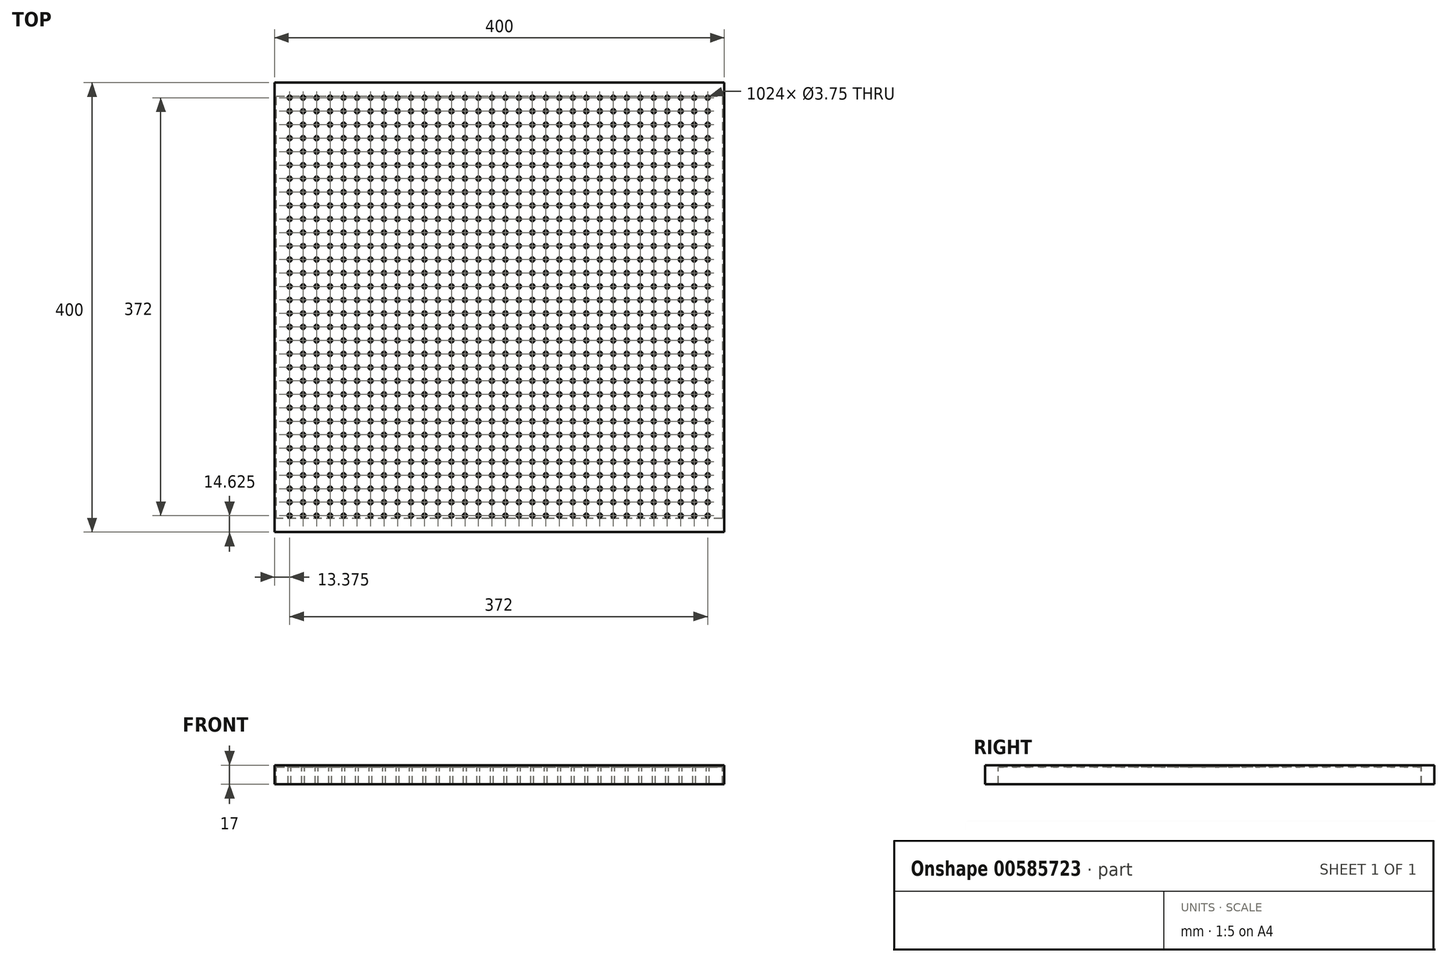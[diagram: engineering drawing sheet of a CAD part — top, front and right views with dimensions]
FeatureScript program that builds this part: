
annotation { "Feature Type Name" : "Feature", "Feature Type Description" : "" }
export const myFeature = defineFeature(function(context is Context, id is Id, definition is map)
    precondition{}
    {
        {
            var Q0;
            Q0=qCreatedBy(makeId("Top.planeOp"),FACE);
            var sketch = newSketch(context, id + "F0", { "sketchPlane" : qUnion([Q0])});
            skLineSegment(sketch, "E0.bottom", {"start": v(200, 200) * mm, "end": v(-200, 200) * mm});
            skLineSegment(sketch, "E0.top", {"start": v(200, -200) * mm, "end": v(-200, -200) * mm});
            skLineSegment(sketch, "E0.left", {"start": v(200, 200) * mm, "end": v(200, -200) * mm});
            skLineSegment(sketch, "E0.right", {"start": v(-200, 200) * mm, "end": v(-200, -200) * mm});
            skPoint(sketch, "E0.middle", {"position": v(0, 0) * mm});
            skSolve(sketch);
        }
        {
            var Q0;
            Q0=makeQuery(id+"F0.imprint","IMPRINT",FACE,{"disambiguationData":[TD([[makeQuery(id+"F0.imprint","IMPRINT",EDGE,{"derivedFrom":sQuery(id+"F0.wireOp",EDGE,"E0.bottom")}),1.0]])]});
            extrude(context, id + "F1", {"entities" : qUnion([Q0]), "depth" : 1.5 * mm, "offsetDistance" : 25 * mm});
        }
        {
            var Q0;
            Q0=makeQuery(id+"F1.opExtrude","CAP_FACE",FACE,{"disambiguationData":[OSD([sQuery(id+"F0.wireOp",EDGE,"E0.bottom"),sQuery(id+"F0.wireOp",EDGE,"E0.top"),sQuery(id+"F0.wireOp",EDGE,"E0.left"),sQuery(id+"F0.wireOp",EDGE,"E0.right")])],"isStart":false});
            var sketch = newSketch(context, id + "F2", { "sketchPlane" : qUnion([Q0])});
            skCircle(sketch, "E1", {"center": v(-186.63, 186.62) * mm, "radius": 1.88 * mm});
            skCircle(sketch, "E2.0.1.0", {"center": v(-186.63, 174.62) * mm, "radius": 1.88 * mm});
            skCircle(sketch, "E2.0.2.0", {"center": v(-186.63, 162.62) * mm, "radius": 1.88 * mm});
            skCircle(sketch, "E2.0.3.0", {"center": v(-186.63, 150.62) * mm, "radius": 1.88 * mm});
            skCircle(sketch, "E2.0.4.0", {"center": v(-186.63, 138.62) * mm, "radius": 1.88 * mm});
            skCircle(sketch, "E2.0.5.0", {"center": v(-186.63, 126.62) * mm, "radius": 1.88 * mm});
            skCircle(sketch, "E2.0.6.0", {"center": v(-186.63, 114.62) * mm, "radius": 1.88 * mm});
            skCircle(sketch, "E2.0.7.0", {"center": v(-186.63, 102.62) * mm, "radius": 1.88 * mm});
            skCircle(sketch, "E2.0.8.0", {"center": v(-186.63, 90.62) * mm, "radius": 1.88 * mm});
            skCircle(sketch, "E2.0.9.0", {"center": v(-186.63, 78.62) * mm, "radius": 1.88 * mm});
            skCircle(sketch, "E2.0.10.0", {"center": v(-186.63, 66.62) * mm, "radius": 1.88 * mm});
            skCircle(sketch, "E2.0.11.0", {"center": v(-186.63, 54.62) * mm, "radius": 1.88 * mm});
            skCircle(sketch, "E2.0.12.0", {"center": v(-186.63, 42.62) * mm, "radius": 1.88 * mm});
            skCircle(sketch, "E2.0.13.0", {"center": v(-186.63, 30.62) * mm, "radius": 1.88 * mm});
            skCircle(sketch, "E2.0.14.0", {"center": v(-186.63, 18.62) * mm, "radius": 1.88 * mm});
            skCircle(sketch, "E2.0.15.0", {"center": v(-186.63, 6.62) * mm, "radius": 1.88 * mm});
            skCircle(sketch, "E2.0.16.0", {"center": v(-186.63, -5.38) * mm, "radius": 1.88 * mm});
            skCircle(sketch, "E2.0.17.0", {"center": v(-186.63, -17.38) * mm, "radius": 1.88 * mm});
            skCircle(sketch, "E2.0.18.0", {"center": v(-186.63, -29.38) * mm, "radius": 1.88 * mm});
            skCircle(sketch, "E2.0.19.0", {"center": v(-186.63, -41.38) * mm, "radius": 1.88 * mm});
            skCircle(sketch, "E2.0.20.0", {"center": v(-186.63, -53.38) * mm, "radius": 1.88 * mm});
            skCircle(sketch, "E2.0.21.0", {"center": v(-186.63, -65.38) * mm, "radius": 1.88 * mm});
            skCircle(sketch, "E2.0.22.0", {"center": v(-186.63, -77.38) * mm, "radius": 1.88 * mm});
            skCircle(sketch, "E2.0.23.0", {"center": v(-186.63, -89.38) * mm, "radius": 1.88 * mm});
            skCircle(sketch, "E2.0.24.0", {"center": v(-186.63, -101.38) * mm, "radius": 1.88 * mm});
            skCircle(sketch, "E2.0.25.0", {"center": v(-186.63, -113.38) * mm, "radius": 1.88 * mm});
            skCircle(sketch, "E2.0.26.0", {"center": v(-186.63, -125.38) * mm, "radius": 1.88 * mm});
            skCircle(sketch, "E2.0.27.0", {"center": v(-186.63, -137.38) * mm, "radius": 1.88 * mm});
            skCircle(sketch, "E2.0.28.0", {"center": v(-186.63, -149.38) * mm, "radius": 1.88 * mm});
            skCircle(sketch, "E2.0.29.0", {"center": v(-186.63, -161.38) * mm, "radius": 1.88 * mm});
            skCircle(sketch, "E2.0.30.0", {"center": v(-186.63, -173.38) * mm, "radius": 1.88 * mm});
            skCircle(sketch, "E2.0.31.0", {"center": v(-186.63, -185.38) * mm, "radius": 1.88 * mm});
            skCircle(sketch, "E2.1.0.0", {"center": v(-174.63, 186.62) * mm, "radius": 1.88 * mm});
            skCircle(sketch, "E2.1.1.0", {"center": v(-174.63, 174.62) * mm, "radius": 1.88 * mm});
            skCircle(sketch, "E2.1.2.0", {"center": v(-174.63, 162.62) * mm, "radius": 1.88 * mm});
            skCircle(sketch, "E2.1.3.0", {"center": v(-174.63, 150.62) * mm, "radius": 1.88 * mm});
            skCircle(sketch, "E2.1.4.0", {"center": v(-174.63, 138.62) * mm, "radius": 1.88 * mm});
            skCircle(sketch, "E2.1.5.0", {"center": v(-174.63, 126.62) * mm, "radius": 1.88 * mm});
            skCircle(sketch, "E2.1.6.0", {"center": v(-174.63, 114.62) * mm, "radius": 1.88 * mm});
            skCircle(sketch, "E2.1.7.0", {"center": v(-174.63, 102.62) * mm, "radius": 1.88 * mm});
            skCircle(sketch, "E2.1.8.0", {"center": v(-174.63, 90.62) * mm, "radius": 1.88 * mm});
            skCircle(sketch, "E2.1.9.0", {"center": v(-174.63, 78.62) * mm, "radius": 1.88 * mm});
            skCircle(sketch, "E2.1.10.0", {"center": v(-174.63, 66.62) * mm, "radius": 1.88 * mm});
            skCircle(sketch, "E2.1.11.0", {"center": v(-174.63, 54.62) * mm, "radius": 1.88 * mm});
            skCircle(sketch, "E2.1.12.0", {"center": v(-174.63, 42.62) * mm, "radius": 1.88 * mm});
            skCircle(sketch, "E2.1.13.0", {"center": v(-174.63, 30.62) * mm, "radius": 1.88 * mm});
            skCircle(sketch, "E2.1.14.0", {"center": v(-174.63, 18.62) * mm, "radius": 1.88 * mm});
            skCircle(sketch, "E2.1.15.0", {"center": v(-174.63, 6.62) * mm, "radius": 1.88 * mm});
            skCircle(sketch, "E2.1.16.0", {"center": v(-174.63, -5.38) * mm, "radius": 1.88 * mm});
            skCircle(sketch, "E2.1.17.0", {"center": v(-174.63, -17.38) * mm, "radius": 1.88 * mm});
            skCircle(sketch, "E2.1.18.0", {"center": v(-174.63, -29.38) * mm, "radius": 1.88 * mm});
            skCircle(sketch, "E2.1.19.0", {"center": v(-174.63, -41.38) * mm, "radius": 1.88 * mm});
            skCircle(sketch, "E2.1.20.0", {"center": v(-174.63, -53.38) * mm, "radius": 1.88 * mm});
            skCircle(sketch, "E2.1.21.0", {"center": v(-174.63, -65.38) * mm, "radius": 1.88 * mm});
            skCircle(sketch, "E2.1.22.0", {"center": v(-174.63, -77.38) * mm, "radius": 1.88 * mm});
            skCircle(sketch, "E2.1.23.0", {"center": v(-174.63, -89.38) * mm, "radius": 1.88 * mm});
            skCircle(sketch, "E2.1.24.0", {"center": v(-174.63, -101.38) * mm, "radius": 1.88 * mm});
            skCircle(sketch, "E2.1.25.0", {"center": v(-174.63, -113.38) * mm, "radius": 1.88 * mm});
            skCircle(sketch, "E2.1.26.0", {"center": v(-174.63, -125.38) * mm, "radius": 1.88 * mm});
            skCircle(sketch, "E2.1.27.0", {"center": v(-174.63, -137.38) * mm, "radius": 1.88 * mm});
            skCircle(sketch, "E2.1.28.0", {"center": v(-174.63, -149.38) * mm, "radius": 1.88 * mm});
            skCircle(sketch, "E2.1.29.0", {"center": v(-174.63, -161.38) * mm, "radius": 1.88 * mm});
            skCircle(sketch, "E2.1.30.0", {"center": v(-174.63, -173.38) * mm, "radius": 1.88 * mm});
            skCircle(sketch, "E2.1.31.0", {"center": v(-174.63, -185.38) * mm, "radius": 1.88 * mm});
            skCircle(sketch, "E2.2.0.0", {"center": v(-162.63, 186.62) * mm, "radius": 1.88 * mm});
            skCircle(sketch, "E2.2.1.0", {"center": v(-162.63, 174.62) * mm, "radius": 1.88 * mm});
            skCircle(sketch, "E2.2.2.0", {"center": v(-162.63, 162.62) * mm, "radius": 1.88 * mm});
            skCircle(sketch, "E2.2.3.0", {"center": v(-162.63, 150.62) * mm, "radius": 1.88 * mm});
            skCircle(sketch, "E2.2.4.0", {"center": v(-162.63, 138.62) * mm, "radius": 1.88 * mm});
            skCircle(sketch, "E2.2.5.0", {"center": v(-162.63, 126.62) * mm, "radius": 1.88 * mm});
            skCircle(sketch, "E2.2.6.0", {"center": v(-162.63, 114.62) * mm, "radius": 1.88 * mm});
            skCircle(sketch, "E2.2.7.0", {"center": v(-162.63, 102.62) * mm, "radius": 1.88 * mm});
            skCircle(sketch, "E2.2.8.0", {"center": v(-162.63, 90.62) * mm, "radius": 1.88 * mm});
            skCircle(sketch, "E2.2.9.0", {"center": v(-162.63, 78.62) * mm, "radius": 1.88 * mm});
            skCircle(sketch, "E2.2.10.0", {"center": v(-162.63, 66.62) * mm, "radius": 1.88 * mm});
            skCircle(sketch, "E2.2.11.0", {"center": v(-162.63, 54.62) * mm, "radius": 1.88 * mm});
            skCircle(sketch, "E2.2.12.0", {"center": v(-162.63, 42.62) * mm, "radius": 1.88 * mm});
            skCircle(sketch, "E2.2.13.0", {"center": v(-162.63, 30.62) * mm, "radius": 1.88 * mm});
            skCircle(sketch, "E2.2.14.0", {"center": v(-162.63, 18.62) * mm, "radius": 1.88 * mm});
            skCircle(sketch, "E2.2.15.0", {"center": v(-162.63, 6.62) * mm, "radius": 1.88 * mm});
            skCircle(sketch, "E2.2.16.0", {"center": v(-162.63, -5.38) * mm, "radius": 1.88 * mm});
            skCircle(sketch, "E2.2.17.0", {"center": v(-162.63, -17.38) * mm, "radius": 1.88 * mm});
            skCircle(sketch, "E2.2.18.0", {"center": v(-162.63, -29.38) * mm, "radius": 1.88 * mm});
            skCircle(sketch, "E2.2.19.0", {"center": v(-162.63, -41.38) * mm, "radius": 1.88 * mm});
            skCircle(sketch, "E2.2.20.0", {"center": v(-162.63, -53.38) * mm, "radius": 1.88 * mm});
            skCircle(sketch, "E2.2.21.0", {"center": v(-162.63, -65.38) * mm, "radius": 1.88 * mm});
            skCircle(sketch, "E2.2.22.0", {"center": v(-162.63, -77.38) * mm, "radius": 1.88 * mm});
            skCircle(sketch, "E2.2.23.0", {"center": v(-162.63, -89.38) * mm, "radius": 1.88 * mm});
            skCircle(sketch, "E2.2.24.0", {"center": v(-162.63, -101.38) * mm, "radius": 1.88 * mm});
            skCircle(sketch, "E2.2.25.0", {"center": v(-162.63, -113.38) * mm, "radius": 1.88 * mm});
            skCircle(sketch, "E2.2.26.0", {"center": v(-162.63, -125.38) * mm, "radius": 1.88 * mm});
            skCircle(sketch, "E2.2.27.0", {"center": v(-162.63, -137.38) * mm, "radius": 1.88 * mm});
            skCircle(sketch, "E2.2.28.0", {"center": v(-162.63, -149.38) * mm, "radius": 1.88 * mm});
            skCircle(sketch, "E2.2.29.0", {"center": v(-162.63, -161.38) * mm, "radius": 1.88 * mm});
            skCircle(sketch, "E2.2.30.0", {"center": v(-162.63, -173.38) * mm, "radius": 1.88 * mm});
            skCircle(sketch, "E2.2.31.0", {"center": v(-162.63, -185.38) * mm, "radius": 1.88 * mm});
            skCircle(sketch, "E2.3.0.0", {"center": v(-150.63, 186.62) * mm, "radius": 1.88 * mm});
            skCircle(sketch, "E2.3.1.0", {"center": v(-150.63, 174.62) * mm, "radius": 1.88 * mm});
            skCircle(sketch, "E2.3.2.0", {"center": v(-150.63, 162.62) * mm, "radius": 1.88 * mm});
            skCircle(sketch, "E2.3.3.0", {"center": v(-150.63, 150.62) * mm, "radius": 1.88 * mm});
            skCircle(sketch, "E2.3.4.0", {"center": v(-150.63, 138.62) * mm, "radius": 1.88 * mm});
            skCircle(sketch, "E2.3.5.0", {"center": v(-150.63, 126.62) * mm, "radius": 1.88 * mm});
            skCircle(sketch, "E2.3.6.0", {"center": v(-150.63, 114.62) * mm, "radius": 1.88 * mm});
            skCircle(sketch, "E2.3.7.0", {"center": v(-150.63, 102.62) * mm, "radius": 1.88 * mm});
            skCircle(sketch, "E2.3.8.0", {"center": v(-150.63, 90.62) * mm, "radius": 1.88 * mm});
            skCircle(sketch, "E2.3.9.0", {"center": v(-150.63, 78.62) * mm, "radius": 1.88 * mm});
            skCircle(sketch, "E2.3.10.0", {"center": v(-150.63, 66.62) * mm, "radius": 1.88 * mm});
            skCircle(sketch, "E2.3.11.0", {"center": v(-150.63, 54.62) * mm, "radius": 1.88 * mm});
            skCircle(sketch, "E2.3.12.0", {"center": v(-150.63, 42.62) * mm, "radius": 1.88 * mm});
            skCircle(sketch, "E2.3.13.0", {"center": v(-150.63, 30.62) * mm, "radius": 1.88 * mm});
            skCircle(sketch, "E2.3.14.0", {"center": v(-150.63, 18.62) * mm, "radius": 1.88 * mm});
            skCircle(sketch, "E2.3.15.0", {"center": v(-150.63, 6.62) * mm, "radius": 1.88 * mm});
            skCircle(sketch, "E2.3.16.0", {"center": v(-150.63, -5.38) * mm, "radius": 1.88 * mm});
            skCircle(sketch, "E2.3.17.0", {"center": v(-150.63, -17.38) * mm, "radius": 1.88 * mm});
            skCircle(sketch, "E2.3.18.0", {"center": v(-150.63, -29.38) * mm, "radius": 1.88 * mm});
            skCircle(sketch, "E2.3.19.0", {"center": v(-150.63, -41.38) * mm, "radius": 1.88 * mm});
            skCircle(sketch, "E2.3.20.0", {"center": v(-150.63, -53.38) * mm, "radius": 1.88 * mm});
            skCircle(sketch, "E2.3.21.0", {"center": v(-150.63, -65.38) * mm, "radius": 1.88 * mm});
            skCircle(sketch, "E2.3.22.0", {"center": v(-150.63, -77.38) * mm, "radius": 1.88 * mm});
            skCircle(sketch, "E2.3.23.0", {"center": v(-150.63, -89.38) * mm, "radius": 1.88 * mm});
            skCircle(sketch, "E2.3.24.0", {"center": v(-150.63, -101.38) * mm, "radius": 1.88 * mm});
            skCircle(sketch, "E2.3.25.0", {"center": v(-150.63, -113.38) * mm, "radius": 1.88 * mm});
            skCircle(sketch, "E2.3.26.0", {"center": v(-150.63, -125.38) * mm, "radius": 1.88 * mm});
            skCircle(sketch, "E2.3.27.0", {"center": v(-150.63, -137.38) * mm, "radius": 1.88 * mm});
            skCircle(sketch, "E2.3.28.0", {"center": v(-150.63, -149.38) * mm, "radius": 1.88 * mm});
            skCircle(sketch, "E2.3.29.0", {"center": v(-150.63, -161.38) * mm, "radius": 1.88 * mm});
            skCircle(sketch, "E2.3.30.0", {"center": v(-150.63, -173.38) * mm, "radius": 1.88 * mm});
            skCircle(sketch, "E2.3.31.0", {"center": v(-150.63, -185.38) * mm, "radius": 1.88 * mm});
            skCircle(sketch, "E2.4.0.0", {"center": v(-138.63, 186.62) * mm, "radius": 1.88 * mm});
            skCircle(sketch, "E2.4.1.0", {"center": v(-138.63, 174.62) * mm, "radius": 1.88 * mm});
            skCircle(sketch, "E2.4.2.0", {"center": v(-138.63, 162.62) * mm, "radius": 1.88 * mm});
            skCircle(sketch, "E2.4.3.0", {"center": v(-138.63, 150.62) * mm, "radius": 1.88 * mm});
            skCircle(sketch, "E2.4.4.0", {"center": v(-138.63, 138.62) * mm, "radius": 1.88 * mm});
            skCircle(sketch, "E2.4.5.0", {"center": v(-138.63, 126.62) * mm, "radius": 1.88 * mm});
            skCircle(sketch, "E2.4.6.0", {"center": v(-138.63, 114.62) * mm, "radius": 1.88 * mm});
            skCircle(sketch, "E2.4.7.0", {"center": v(-138.63, 102.62) * mm, "radius": 1.88 * mm});
            skCircle(sketch, "E2.4.8.0", {"center": v(-138.63, 90.62) * mm, "radius": 1.88 * mm});
            skCircle(sketch, "E2.4.9.0", {"center": v(-138.63, 78.62) * mm, "radius": 1.88 * mm});
            skCircle(sketch, "E2.4.10.0", {"center": v(-138.63, 66.62) * mm, "radius": 1.88 * mm});
            skCircle(sketch, "E2.4.11.0", {"center": v(-138.63, 54.62) * mm, "radius": 1.88 * mm});
            skCircle(sketch, "E2.4.12.0", {"center": v(-138.63, 42.62) * mm, "radius": 1.88 * mm});
            skCircle(sketch, "E2.4.13.0", {"center": v(-138.63, 30.62) * mm, "radius": 1.88 * mm});
            skCircle(sketch, "E2.4.14.0", {"center": v(-138.63, 18.62) * mm, "radius": 1.88 * mm});
            skCircle(sketch, "E2.4.15.0", {"center": v(-138.63, 6.62) * mm, "radius": 1.88 * mm});
            skCircle(sketch, "E2.4.16.0", {"center": v(-138.63, -5.38) * mm, "radius": 1.88 * mm});
            skCircle(sketch, "E2.4.17.0", {"center": v(-138.63, -17.38) * mm, "radius": 1.88 * mm});
            skCircle(sketch, "E2.4.18.0", {"center": v(-138.63, -29.38) * mm, "radius": 1.88 * mm});
            skCircle(sketch, "E2.4.19.0", {"center": v(-138.63, -41.38) * mm, "radius": 1.88 * mm});
            skCircle(sketch, "E2.4.20.0", {"center": v(-138.63, -53.38) * mm, "radius": 1.88 * mm});
            skCircle(sketch, "E2.4.21.0", {"center": v(-138.63, -65.38) * mm, "radius": 1.88 * mm});
            skCircle(sketch, "E2.4.22.0", {"center": v(-138.63, -77.38) * mm, "radius": 1.88 * mm});
            skCircle(sketch, "E2.4.23.0", {"center": v(-138.63, -89.38) * mm, "radius": 1.88 * mm});
            skCircle(sketch, "E2.4.24.0", {"center": v(-138.63, -101.38) * mm, "radius": 1.88 * mm});
            skCircle(sketch, "E2.4.25.0", {"center": v(-138.63, -113.38) * mm, "radius": 1.88 * mm});
            skCircle(sketch, "E2.4.26.0", {"center": v(-138.63, -125.38) * mm, "radius": 1.88 * mm});
            skCircle(sketch, "E2.4.27.0", {"center": v(-138.63, -137.38) * mm, "radius": 1.88 * mm});
            skCircle(sketch, "E2.4.28.0", {"center": v(-138.63, -149.38) * mm, "radius": 1.88 * mm});
            skCircle(sketch, "E2.4.29.0", {"center": v(-138.63, -161.38) * mm, "radius": 1.88 * mm});
            skCircle(sketch, "E2.4.30.0", {"center": v(-138.63, -173.38) * mm, "radius": 1.88 * mm});
            skCircle(sketch, "E2.4.31.0", {"center": v(-138.63, -185.38) * mm, "radius": 1.88 * mm});
            skCircle(sketch, "E2.5.0.0", {"center": v(-126.63, 186.62) * mm, "radius": 1.88 * mm});
            skCircle(sketch, "E2.5.1.0", {"center": v(-126.63, 174.62) * mm, "radius": 1.88 * mm});
            skCircle(sketch, "E2.5.2.0", {"center": v(-126.63, 162.62) * mm, "radius": 1.88 * mm});
            skCircle(sketch, "E2.5.3.0", {"center": v(-126.63, 150.62) * mm, "radius": 1.88 * mm});
            skCircle(sketch, "E2.5.4.0", {"center": v(-126.63, 138.62) * mm, "radius": 1.88 * mm});
            skCircle(sketch, "E2.5.5.0", {"center": v(-126.63, 126.62) * mm, "radius": 1.88 * mm});
            skCircle(sketch, "E2.5.6.0", {"center": v(-126.63, 114.62) * mm, "radius": 1.88 * mm});
            skCircle(sketch, "E2.5.7.0", {"center": v(-126.63, 102.62) * mm, "radius": 1.88 * mm});
            skCircle(sketch, "E2.5.8.0", {"center": v(-126.63, 90.62) * mm, "radius": 1.88 * mm});
            skCircle(sketch, "E2.5.9.0", {"center": v(-126.63, 78.62) * mm, "radius": 1.88 * mm});
            skCircle(sketch, "E2.5.10.0", {"center": v(-126.63, 66.62) * mm, "radius": 1.88 * mm});
            skCircle(sketch, "E2.5.11.0", {"center": v(-126.63, 54.62) * mm, "radius": 1.88 * mm});
            skCircle(sketch, "E2.5.12.0", {"center": v(-126.63, 42.62) * mm, "radius": 1.88 * mm});
            skCircle(sketch, "E2.5.13.0", {"center": v(-126.63, 30.62) * mm, "radius": 1.88 * mm});
            skCircle(sketch, "E2.5.14.0", {"center": v(-126.63, 18.62) * mm, "radius": 1.88 * mm});
            skCircle(sketch, "E2.5.15.0", {"center": v(-126.63, 6.62) * mm, "radius": 1.88 * mm});
            skCircle(sketch, "E2.5.16.0", {"center": v(-126.63, -5.38) * mm, "radius": 1.88 * mm});
            skCircle(sketch, "E2.5.17.0", {"center": v(-126.63, -17.38) * mm, "radius": 1.88 * mm});
            skCircle(sketch, "E2.5.18.0", {"center": v(-126.63, -29.38) * mm, "radius": 1.88 * mm});
            skCircle(sketch, "E2.5.19.0", {"center": v(-126.63, -41.38) * mm, "radius": 1.88 * mm});
            skCircle(sketch, "E2.5.20.0", {"center": v(-126.63, -53.38) * mm, "radius": 1.88 * mm});
            skCircle(sketch, "E2.5.21.0", {"center": v(-126.63, -65.38) * mm, "radius": 1.88 * mm});
            skCircle(sketch, "E2.5.22.0", {"center": v(-126.63, -77.38) * mm, "radius": 1.88 * mm});
            skCircle(sketch, "E2.5.23.0", {"center": v(-126.63, -89.38) * mm, "radius": 1.88 * mm});
            skCircle(sketch, "E2.5.24.0", {"center": v(-126.63, -101.38) * mm, "radius": 1.88 * mm});
            skCircle(sketch, "E2.5.25.0", {"center": v(-126.63, -113.38) * mm, "radius": 1.88 * mm});
            skCircle(sketch, "E2.5.26.0", {"center": v(-126.63, -125.38) * mm, "radius": 1.88 * mm});
            skCircle(sketch, "E2.5.27.0", {"center": v(-126.63, -137.38) * mm, "radius": 1.88 * mm});
            skCircle(sketch, "E2.5.28.0", {"center": v(-126.63, -149.38) * mm, "radius": 1.88 * mm});
            skCircle(sketch, "E2.5.29.0", {"center": v(-126.63, -161.38) * mm, "radius": 1.88 * mm});
            skCircle(sketch, "E2.5.30.0", {"center": v(-126.63, -173.38) * mm, "radius": 1.88 * mm});
            skCircle(sketch, "E2.5.31.0", {"center": v(-126.63, -185.38) * mm, "radius": 1.88 * mm});
            skCircle(sketch, "E2.6.0.0", {"center": v(-114.62, 186.62) * mm, "radius": 1.88 * mm});
            skCircle(sketch, "E2.6.1.0", {"center": v(-114.62, 174.62) * mm, "radius": 1.88 * mm});
            skCircle(sketch, "E2.6.2.0", {"center": v(-114.62, 162.62) * mm, "radius": 1.88 * mm});
            skCircle(sketch, "E2.6.3.0", {"center": v(-114.62, 150.62) * mm, "radius": 1.88 * mm});
            skCircle(sketch, "E2.6.4.0", {"center": v(-114.62, 138.62) * mm, "radius": 1.88 * mm});
            skCircle(sketch, "E2.6.5.0", {"center": v(-114.62, 126.62) * mm, "radius": 1.88 * mm});
            skCircle(sketch, "E2.6.6.0", {"center": v(-114.62, 114.62) * mm, "radius": 1.88 * mm});
            skCircle(sketch, "E2.6.7.0", {"center": v(-114.62, 102.62) * mm, "radius": 1.88 * mm});
            skCircle(sketch, "E2.6.8.0", {"center": v(-114.62, 90.62) * mm, "radius": 1.88 * mm});
            skCircle(sketch, "E2.6.9.0", {"center": v(-114.62, 78.62) * mm, "radius": 1.88 * mm});
            skCircle(sketch, "E2.6.10.0", {"center": v(-114.62, 66.62) * mm, "radius": 1.88 * mm});
            skCircle(sketch, "E2.6.11.0", {"center": v(-114.62, 54.62) * mm, "radius": 1.88 * mm});
            skCircle(sketch, "E2.6.12.0", {"center": v(-114.62, 42.62) * mm, "radius": 1.88 * mm});
            skCircle(sketch, "E2.6.13.0", {"center": v(-114.62, 30.62) * mm, "radius": 1.88 * mm});
            skCircle(sketch, "E2.6.14.0", {"center": v(-114.62, 18.62) * mm, "radius": 1.88 * mm});
            skCircle(sketch, "E2.6.15.0", {"center": v(-114.62, 6.62) * mm, "radius": 1.88 * mm});
            skCircle(sketch, "E2.6.16.0", {"center": v(-114.62, -5.38) * mm, "radius": 1.88 * mm});
            skCircle(sketch, "E2.6.17.0", {"center": v(-114.62, -17.38) * mm, "radius": 1.88 * mm});
            skCircle(sketch, "E2.6.18.0", {"center": v(-114.62, -29.38) * mm, "radius": 1.88 * mm});
            skCircle(sketch, "E2.6.19.0", {"center": v(-114.62, -41.38) * mm, "radius": 1.88 * mm});
            skCircle(sketch, "E2.6.20.0", {"center": v(-114.62, -53.38) * mm, "radius": 1.88 * mm});
            skCircle(sketch, "E2.6.21.0", {"center": v(-114.62, -65.38) * mm, "radius": 1.88 * mm});
            skCircle(sketch, "E2.6.22.0", {"center": v(-114.62, -77.38) * mm, "radius": 1.88 * mm});
            skCircle(sketch, "E2.6.23.0", {"center": v(-114.62, -89.38) * mm, "radius": 1.88 * mm});
            skCircle(sketch, "E2.6.24.0", {"center": v(-114.62, -101.38) * mm, "radius": 1.88 * mm});
            skCircle(sketch, "E2.6.25.0", {"center": v(-114.62, -113.38) * mm, "radius": 1.88 * mm});
            skCircle(sketch, "E2.6.26.0", {"center": v(-114.62, -125.38) * mm, "radius": 1.88 * mm});
            skCircle(sketch, "E2.6.27.0", {"center": v(-114.62, -137.38) * mm, "radius": 1.88 * mm});
            skCircle(sketch, "E2.6.28.0", {"center": v(-114.62, -149.38) * mm, "radius": 1.88 * mm});
            skCircle(sketch, "E2.6.29.0", {"center": v(-114.62, -161.38) * mm, "radius": 1.88 * mm});
            skCircle(sketch, "E2.6.30.0", {"center": v(-114.62, -173.38) * mm, "radius": 1.88 * mm});
            skCircle(sketch, "E2.6.31.0", {"center": v(-114.62, -185.38) * mm, "radius": 1.88 * mm});
            skCircle(sketch, "E2.7.0.0", {"center": v(-102.62, 186.62) * mm, "radius": 1.88 * mm});
            skCircle(sketch, "E2.7.1.0", {"center": v(-102.62, 174.62) * mm, "radius": 1.88 * mm});
            skCircle(sketch, "E2.7.2.0", {"center": v(-102.62, 162.62) * mm, "radius": 1.88 * mm});
            skCircle(sketch, "E2.7.3.0", {"center": v(-102.62, 150.62) * mm, "radius": 1.88 * mm});
            skCircle(sketch, "E2.7.4.0", {"center": v(-102.62, 138.62) * mm, "radius": 1.88 * mm});
            skCircle(sketch, "E2.7.5.0", {"center": v(-102.62, 126.62) * mm, "radius": 1.88 * mm});
            skCircle(sketch, "E2.7.6.0", {"center": v(-102.62, 114.62) * mm, "radius": 1.88 * mm});
            skCircle(sketch, "E2.7.7.0", {"center": v(-102.62, 102.62) * mm, "radius": 1.88 * mm});
            skCircle(sketch, "E2.7.8.0", {"center": v(-102.62, 90.62) * mm, "radius": 1.88 * mm});
            skCircle(sketch, "E2.7.9.0", {"center": v(-102.62, 78.62) * mm, "radius": 1.88 * mm});
            skCircle(sketch, "E2.7.10.0", {"center": v(-102.62, 66.62) * mm, "radius": 1.88 * mm});
            skCircle(sketch, "E2.7.11.0", {"center": v(-102.62, 54.62) * mm, "radius": 1.88 * mm});
            skCircle(sketch, "E2.7.12.0", {"center": v(-102.62, 42.62) * mm, "radius": 1.88 * mm});
            skCircle(sketch, "E2.7.13.0", {"center": v(-102.62, 30.62) * mm, "radius": 1.88 * mm});
            skCircle(sketch, "E2.7.14.0", {"center": v(-102.62, 18.62) * mm, "radius": 1.88 * mm});
            skCircle(sketch, "E2.7.15.0", {"center": v(-102.62, 6.62) * mm, "radius": 1.88 * mm});
            skCircle(sketch, "E2.7.16.0", {"center": v(-102.62, -5.38) * mm, "radius": 1.88 * mm});
            skCircle(sketch, "E2.7.17.0", {"center": v(-102.62, -17.38) * mm, "radius": 1.88 * mm});
            skCircle(sketch, "E2.7.18.0", {"center": v(-102.62, -29.38) * mm, "radius": 1.88 * mm});
            skCircle(sketch, "E2.7.19.0", {"center": v(-102.62, -41.38) * mm, "radius": 1.88 * mm});
            skCircle(sketch, "E2.7.20.0", {"center": v(-102.62, -53.38) * mm, "radius": 1.88 * mm});
            skCircle(sketch, "E2.7.21.0", {"center": v(-102.62, -65.38) * mm, "radius": 1.88 * mm});
            skCircle(sketch, "E2.7.22.0", {"center": v(-102.62, -77.38) * mm, "radius": 1.88 * mm});
            skCircle(sketch, "E2.7.23.0", {"center": v(-102.62, -89.38) * mm, "radius": 1.88 * mm});
            skCircle(sketch, "E2.7.24.0", {"center": v(-102.62, -101.38) * mm, "radius": 1.88 * mm});
            skCircle(sketch, "E2.7.25.0", {"center": v(-102.62, -113.38) * mm, "radius": 1.88 * mm});
            skCircle(sketch, "E2.7.26.0", {"center": v(-102.62, -125.38) * mm, "radius": 1.88 * mm});
            skCircle(sketch, "E2.7.27.0", {"center": v(-102.62, -137.38) * mm, "radius": 1.88 * mm});
            skCircle(sketch, "E2.7.28.0", {"center": v(-102.62, -149.38) * mm, "radius": 1.88 * mm});
            skCircle(sketch, "E2.7.29.0", {"center": v(-102.62, -161.38) * mm, "radius": 1.88 * mm});
            skCircle(sketch, "E2.7.30.0", {"center": v(-102.62, -173.38) * mm, "radius": 1.88 * mm});
            skCircle(sketch, "E2.7.31.0", {"center": v(-102.62, -185.38) * mm, "radius": 1.88 * mm});
            skCircle(sketch, "E2.8.0.0", {"center": v(-90.62, 186.62) * mm, "radius": 1.88 * mm});
            skCircle(sketch, "E2.8.1.0", {"center": v(-90.62, 174.62) * mm, "radius": 1.88 * mm});
            skCircle(sketch, "E2.8.2.0", {"center": v(-90.62, 162.62) * mm, "radius": 1.88 * mm});
            skCircle(sketch, "E2.8.3.0", {"center": v(-90.62, 150.62) * mm, "radius": 1.88 * mm});
            skCircle(sketch, "E2.8.4.0", {"center": v(-90.62, 138.62) * mm, "radius": 1.88 * mm});
            skCircle(sketch, "E2.8.5.0", {"center": v(-90.62, 126.62) * mm, "radius": 1.88 * mm});
            skCircle(sketch, "E2.8.6.0", {"center": v(-90.62, 114.62) * mm, "radius": 1.88 * mm});
            skCircle(sketch, "E2.8.7.0", {"center": v(-90.62, 102.62) * mm, "radius": 1.88 * mm});
            skCircle(sketch, "E2.8.8.0", {"center": v(-90.62, 90.62) * mm, "radius": 1.88 * mm});
            skCircle(sketch, "E2.8.9.0", {"center": v(-90.62, 78.62) * mm, "radius": 1.88 * mm});
            skCircle(sketch, "E2.8.10.0", {"center": v(-90.62, 66.62) * mm, "radius": 1.88 * mm});
            skCircle(sketch, "E2.8.11.0", {"center": v(-90.62, 54.62) * mm, "radius": 1.88 * mm});
            skCircle(sketch, "E2.8.12.0", {"center": v(-90.62, 42.62) * mm, "radius": 1.88 * mm});
            skCircle(sketch, "E2.8.13.0", {"center": v(-90.62, 30.62) * mm, "radius": 1.88 * mm});
            skCircle(sketch, "E2.8.14.0", {"center": v(-90.62, 18.62) * mm, "radius": 1.88 * mm});
            skCircle(sketch, "E2.8.15.0", {"center": v(-90.62, 6.62) * mm, "radius": 1.88 * mm});
            skCircle(sketch, "E2.8.16.0", {"center": v(-90.62, -5.38) * mm, "radius": 1.88 * mm});
            skCircle(sketch, "E2.8.17.0", {"center": v(-90.62, -17.38) * mm, "radius": 1.88 * mm});
            skCircle(sketch, "E2.8.18.0", {"center": v(-90.62, -29.38) * mm, "radius": 1.88 * mm});
            skCircle(sketch, "E2.8.19.0", {"center": v(-90.62, -41.38) * mm, "radius": 1.88 * mm});
            skCircle(sketch, "E2.8.20.0", {"center": v(-90.62, -53.38) * mm, "radius": 1.88 * mm});
            skCircle(sketch, "E2.8.21.0", {"center": v(-90.62, -65.38) * mm, "radius": 1.88 * mm});
            skCircle(sketch, "E2.8.22.0", {"center": v(-90.62, -77.38) * mm, "radius": 1.88 * mm});
            skCircle(sketch, "E2.8.23.0", {"center": v(-90.62, -89.38) * mm, "radius": 1.88 * mm});
            skCircle(sketch, "E2.8.24.0", {"center": v(-90.62, -101.38) * mm, "radius": 1.88 * mm});
            skCircle(sketch, "E2.8.25.0", {"center": v(-90.62, -113.38) * mm, "radius": 1.88 * mm});
            skCircle(sketch, "E2.8.26.0", {"center": v(-90.62, -125.38) * mm, "radius": 1.88 * mm});
            skCircle(sketch, "E2.8.27.0", {"center": v(-90.62, -137.38) * mm, "radius": 1.88 * mm});
            skCircle(sketch, "E2.8.28.0", {"center": v(-90.62, -149.38) * mm, "radius": 1.88 * mm});
            skCircle(sketch, "E2.8.29.0", {"center": v(-90.62, -161.38) * mm, "radius": 1.88 * mm});
            skCircle(sketch, "E2.8.30.0", {"center": v(-90.62, -173.38) * mm, "radius": 1.88 * mm});
            skCircle(sketch, "E2.8.31.0", {"center": v(-90.62, -185.38) * mm, "radius": 1.88 * mm});
            skCircle(sketch, "E2.9.0.0", {"center": v(-78.62, 186.62) * mm, "radius": 1.88 * mm});
            skCircle(sketch, "E2.9.1.0", {"center": v(-78.62, 174.62) * mm, "radius": 1.88 * mm});
            skCircle(sketch, "E2.9.2.0", {"center": v(-78.62, 162.62) * mm, "radius": 1.88 * mm});
            skCircle(sketch, "E2.9.3.0", {"center": v(-78.62, 150.62) * mm, "radius": 1.88 * mm});
            skCircle(sketch, "E2.9.4.0", {"center": v(-78.62, 138.62) * mm, "radius": 1.88 * mm});
            skCircle(sketch, "E2.9.5.0", {"center": v(-78.62, 126.62) * mm, "radius": 1.88 * mm});
            skCircle(sketch, "E2.9.6.0", {"center": v(-78.62, 114.62) * mm, "radius": 1.88 * mm});
            skCircle(sketch, "E2.9.7.0", {"center": v(-78.62, 102.62) * mm, "radius": 1.88 * mm});
            skCircle(sketch, "E2.9.8.0", {"center": v(-78.62, 90.62) * mm, "radius": 1.88 * mm});
            skCircle(sketch, "E2.9.9.0", {"center": v(-78.62, 78.62) * mm, "radius": 1.88 * mm});
            skCircle(sketch, "E2.9.10.0", {"center": v(-78.62, 66.62) * mm, "radius": 1.88 * mm});
            skCircle(sketch, "E2.9.11.0", {"center": v(-78.62, 54.62) * mm, "radius": 1.88 * mm});
            skCircle(sketch, "E2.9.12.0", {"center": v(-78.62, 42.62) * mm, "radius": 1.88 * mm});
            skCircle(sketch, "E2.9.13.0", {"center": v(-78.62, 30.62) * mm, "radius": 1.88 * mm});
            skCircle(sketch, "E2.9.14.0", {"center": v(-78.62, 18.62) * mm, "radius": 1.88 * mm});
            skCircle(sketch, "E2.9.15.0", {"center": v(-78.62, 6.62) * mm, "radius": 1.88 * mm});
            skCircle(sketch, "E2.9.16.0", {"center": v(-78.62, -5.38) * mm, "radius": 1.88 * mm});
            skCircle(sketch, "E2.9.17.0", {"center": v(-78.62, -17.38) * mm, "radius": 1.88 * mm});
            skCircle(sketch, "E2.9.18.0", {"center": v(-78.62, -29.38) * mm, "radius": 1.88 * mm});
            skCircle(sketch, "E2.9.19.0", {"center": v(-78.62, -41.38) * mm, "radius": 1.88 * mm});
            skCircle(sketch, "E2.9.20.0", {"center": v(-78.62, -53.38) * mm, "radius": 1.88 * mm});
            skCircle(sketch, "E2.9.21.0", {"center": v(-78.62, -65.38) * mm, "radius": 1.88 * mm});
            skCircle(sketch, "E2.9.22.0", {"center": v(-78.62, -77.38) * mm, "radius": 1.88 * mm});
            skCircle(sketch, "E2.9.23.0", {"center": v(-78.62, -89.38) * mm, "radius": 1.88 * mm});
            skCircle(sketch, "E2.9.24.0", {"center": v(-78.62, -101.38) * mm, "radius": 1.88 * mm});
            skCircle(sketch, "E2.9.25.0", {"center": v(-78.62, -113.38) * mm, "radius": 1.88 * mm});
            skCircle(sketch, "E2.9.26.0", {"center": v(-78.62, -125.38) * mm, "radius": 1.88 * mm});
            skCircle(sketch, "E2.9.27.0", {"center": v(-78.62, -137.38) * mm, "radius": 1.88 * mm});
            skCircle(sketch, "E2.9.28.0", {"center": v(-78.62, -149.38) * mm, "radius": 1.88 * mm});
            skCircle(sketch, "E2.9.29.0", {"center": v(-78.62, -161.38) * mm, "radius": 1.88 * mm});
            skCircle(sketch, "E2.9.30.0", {"center": v(-78.62, -173.38) * mm, "radius": 1.88 * mm});
            skCircle(sketch, "E2.9.31.0", {"center": v(-78.62, -185.38) * mm, "radius": 1.88 * mm});
            skCircle(sketch, "E2.10.0.0", {"center": v(-66.62, 186.62) * mm, "radius": 1.88 * mm});
            skCircle(sketch, "E2.10.1.0", {"center": v(-66.62, 174.62) * mm, "radius": 1.88 * mm});
            skCircle(sketch, "E2.10.2.0", {"center": v(-66.62, 162.62) * mm, "radius": 1.88 * mm});
            skCircle(sketch, "E2.10.3.0", {"center": v(-66.62, 150.62) * mm, "radius": 1.88 * mm});
            skCircle(sketch, "E2.10.4.0", {"center": v(-66.62, 138.62) * mm, "radius": 1.88 * mm});
            skCircle(sketch, "E2.10.5.0", {"center": v(-66.62, 126.62) * mm, "radius": 1.88 * mm});
            skCircle(sketch, "E2.10.6.0", {"center": v(-66.62, 114.62) * mm, "radius": 1.88 * mm});
            skCircle(sketch, "E2.10.7.0", {"center": v(-66.62, 102.62) * mm, "radius": 1.88 * mm});
            skCircle(sketch, "E2.10.8.0", {"center": v(-66.62, 90.62) * mm, "radius": 1.88 * mm});
            skCircle(sketch, "E2.10.9.0", {"center": v(-66.62, 78.62) * mm, "radius": 1.88 * mm});
            skCircle(sketch, "E2.10.10.0", {"center": v(-66.62, 66.62) * mm, "radius": 1.88 * mm});
            skCircle(sketch, "E2.10.11.0", {"center": v(-66.62, 54.62) * mm, "radius": 1.88 * mm});
            skCircle(sketch, "E2.10.12.0", {"center": v(-66.62, 42.62) * mm, "radius": 1.88 * mm});
            skCircle(sketch, "E2.10.13.0", {"center": v(-66.62, 30.62) * mm, "radius": 1.88 * mm});
            skCircle(sketch, "E2.10.14.0", {"center": v(-66.62, 18.62) * mm, "radius": 1.88 * mm});
            skCircle(sketch, "E2.10.15.0", {"center": v(-66.62, 6.62) * mm, "radius": 1.88 * mm});
            skCircle(sketch, "E2.10.16.0", {"center": v(-66.62, -5.38) * mm, "radius": 1.88 * mm});
            skCircle(sketch, "E2.10.17.0", {"center": v(-66.62, -17.38) * mm, "radius": 1.88 * mm});
            skCircle(sketch, "E2.10.18.0", {"center": v(-66.62, -29.38) * mm, "radius": 1.88 * mm});
            skCircle(sketch, "E2.10.19.0", {"center": v(-66.62, -41.38) * mm, "radius": 1.88 * mm});
            skCircle(sketch, "E2.10.20.0", {"center": v(-66.62, -53.38) * mm, "radius": 1.88 * mm});
            skCircle(sketch, "E2.10.21.0", {"center": v(-66.62, -65.38) * mm, "radius": 1.88 * mm});
            skCircle(sketch, "E2.10.22.0", {"center": v(-66.62, -77.38) * mm, "radius": 1.88 * mm});
            skCircle(sketch, "E2.10.23.0", {"center": v(-66.62, -89.38) * mm, "radius": 1.88 * mm});
            skCircle(sketch, "E2.10.24.0", {"center": v(-66.62, -101.38) * mm, "radius": 1.88 * mm});
            skCircle(sketch, "E2.10.25.0", {"center": v(-66.62, -113.38) * mm, "radius": 1.88 * mm});
            skCircle(sketch, "E2.10.26.0", {"center": v(-66.62, -125.38) * mm, "radius": 1.88 * mm});
            skCircle(sketch, "E2.10.27.0", {"center": v(-66.62, -137.38) * mm, "radius": 1.88 * mm});
            skCircle(sketch, "E2.10.28.0", {"center": v(-66.62, -149.38) * mm, "radius": 1.88 * mm});
            skCircle(sketch, "E2.10.29.0", {"center": v(-66.62, -161.38) * mm, "radius": 1.88 * mm});
            skCircle(sketch, "E2.10.30.0", {"center": v(-66.62, -173.38) * mm, "radius": 1.88 * mm});
            skCircle(sketch, "E2.10.31.0", {"center": v(-66.62, -185.38) * mm, "radius": 1.88 * mm});
            skCircle(sketch, "E2.11.0.0", {"center": v(-54.62, 186.62) * mm, "radius": 1.88 * mm});
            skCircle(sketch, "E2.11.1.0", {"center": v(-54.62, 174.62) * mm, "radius": 1.88 * mm});
            skCircle(sketch, "E2.11.2.0", {"center": v(-54.62, 162.62) * mm, "radius": 1.88 * mm});
            skCircle(sketch, "E2.11.3.0", {"center": v(-54.62, 150.62) * mm, "radius": 1.88 * mm});
            skCircle(sketch, "E2.11.4.0", {"center": v(-54.62, 138.62) * mm, "radius": 1.88 * mm});
            skCircle(sketch, "E2.11.5.0", {"center": v(-54.62, 126.62) * mm, "radius": 1.88 * mm});
            skCircle(sketch, "E2.11.6.0", {"center": v(-54.62, 114.62) * mm, "radius": 1.88 * mm});
            skCircle(sketch, "E2.11.7.0", {"center": v(-54.62, 102.62) * mm, "radius": 1.88 * mm});
            skCircle(sketch, "E2.11.8.0", {"center": v(-54.62, 90.62) * mm, "radius": 1.88 * mm});
            skCircle(sketch, "E2.11.9.0", {"center": v(-54.62, 78.62) * mm, "radius": 1.88 * mm});
            skCircle(sketch, "E2.11.10.0", {"center": v(-54.62, 66.62) * mm, "radius": 1.88 * mm});
            skCircle(sketch, "E2.11.11.0", {"center": v(-54.62, 54.62) * mm, "radius": 1.88 * mm});
            skCircle(sketch, "E2.11.12.0", {"center": v(-54.62, 42.62) * mm, "radius": 1.88 * mm});
            skCircle(sketch, "E2.11.13.0", {"center": v(-54.62, 30.62) * mm, "radius": 1.88 * mm});
            skCircle(sketch, "E2.11.14.0", {"center": v(-54.62, 18.62) * mm, "radius": 1.88 * mm});
            skCircle(sketch, "E2.11.15.0", {"center": v(-54.62, 6.62) * mm, "radius": 1.88 * mm});
            skCircle(sketch, "E2.11.16.0", {"center": v(-54.62, -5.38) * mm, "radius": 1.88 * mm});
            skCircle(sketch, "E2.11.17.0", {"center": v(-54.62, -17.38) * mm, "radius": 1.88 * mm});
            skCircle(sketch, "E2.11.18.0", {"center": v(-54.62, -29.38) * mm, "radius": 1.88 * mm});
            skCircle(sketch, "E2.11.19.0", {"center": v(-54.62, -41.38) * mm, "radius": 1.88 * mm});
            skCircle(sketch, "E2.11.20.0", {"center": v(-54.62, -53.38) * mm, "radius": 1.88 * mm});
            skCircle(sketch, "E2.11.21.0", {"center": v(-54.62, -65.38) * mm, "radius": 1.88 * mm});
            skCircle(sketch, "E2.11.22.0", {"center": v(-54.62, -77.38) * mm, "radius": 1.88 * mm});
            skCircle(sketch, "E2.11.23.0", {"center": v(-54.62, -89.38) * mm, "radius": 1.88 * mm});
            skCircle(sketch, "E2.11.24.0", {"center": v(-54.62, -101.38) * mm, "radius": 1.88 * mm});
            skCircle(sketch, "E2.11.25.0", {"center": v(-54.62, -113.38) * mm, "radius": 1.88 * mm});
            skCircle(sketch, "E2.11.26.0", {"center": v(-54.62, -125.38) * mm, "radius": 1.88 * mm});
            skCircle(sketch, "E2.11.27.0", {"center": v(-54.62, -137.38) * mm, "radius": 1.88 * mm});
            skCircle(sketch, "E2.11.28.0", {"center": v(-54.62, -149.38) * mm, "radius": 1.88 * mm});
            skCircle(sketch, "E2.11.29.0", {"center": v(-54.62, -161.38) * mm, "radius": 1.88 * mm});
            skCircle(sketch, "E2.11.30.0", {"center": v(-54.62, -173.38) * mm, "radius": 1.88 * mm});
            skCircle(sketch, "E2.11.31.0", {"center": v(-54.62, -185.38) * mm, "radius": 1.88 * mm});
            skCircle(sketch, "E2.12.0.0", {"center": v(-42.62, 186.62) * mm, "radius": 1.88 * mm});
            skCircle(sketch, "E2.12.1.0", {"center": v(-42.62, 174.62) * mm, "radius": 1.88 * mm});
            skCircle(sketch, "E2.12.2.0", {"center": v(-42.62, 162.62) * mm, "radius": 1.88 * mm});
            skCircle(sketch, "E2.12.3.0", {"center": v(-42.62, 150.62) * mm, "radius": 1.88 * mm});
            skCircle(sketch, "E2.12.4.0", {"center": v(-42.62, 138.62) * mm, "radius": 1.88 * mm});
            skCircle(sketch, "E2.12.5.0", {"center": v(-42.62, 126.62) * mm, "radius": 1.88 * mm});
            skCircle(sketch, "E2.12.6.0", {"center": v(-42.62, 114.62) * mm, "radius": 1.88 * mm});
            skCircle(sketch, "E2.12.7.0", {"center": v(-42.62, 102.62) * mm, "radius": 1.88 * mm});
            skCircle(sketch, "E2.12.8.0", {"center": v(-42.62, 90.62) * mm, "radius": 1.88 * mm});
            skCircle(sketch, "E2.12.9.0", {"center": v(-42.62, 78.62) * mm, "radius": 1.88 * mm});
            skCircle(sketch, "E2.12.10.0", {"center": v(-42.62, 66.62) * mm, "radius": 1.88 * mm});
            skCircle(sketch, "E2.12.11.0", {"center": v(-42.62, 54.62) * mm, "radius": 1.88 * mm});
            skCircle(sketch, "E2.12.12.0", {"center": v(-42.62, 42.62) * mm, "radius": 1.88 * mm});
            skCircle(sketch, "E2.12.13.0", {"center": v(-42.62, 30.62) * mm, "radius": 1.88 * mm});
            skCircle(sketch, "E2.12.14.0", {"center": v(-42.62, 18.62) * mm, "radius": 1.88 * mm});
            skCircle(sketch, "E2.12.15.0", {"center": v(-42.62, 6.62) * mm, "radius": 1.88 * mm});
            skCircle(sketch, "E2.12.16.0", {"center": v(-42.62, -5.38) * mm, "radius": 1.88 * mm});
            skCircle(sketch, "E2.12.17.0", {"center": v(-42.62, -17.38) * mm, "radius": 1.88 * mm});
            skCircle(sketch, "E2.12.18.0", {"center": v(-42.62, -29.38) * mm, "radius": 1.88 * mm});
            skCircle(sketch, "E2.12.19.0", {"center": v(-42.62, -41.38) * mm, "radius": 1.88 * mm});
            skCircle(sketch, "E2.12.20.0", {"center": v(-42.62, -53.38) * mm, "radius": 1.88 * mm});
            skCircle(sketch, "E2.12.21.0", {"center": v(-42.62, -65.38) * mm, "radius": 1.88 * mm});
            skCircle(sketch, "E2.12.22.0", {"center": v(-42.62, -77.38) * mm, "radius": 1.88 * mm});
            skCircle(sketch, "E2.12.23.0", {"center": v(-42.62, -89.38) * mm, "radius": 1.88 * mm});
            skCircle(sketch, "E2.12.24.0", {"center": v(-42.62, -101.38) * mm, "radius": 1.88 * mm});
            skCircle(sketch, "E2.12.25.0", {"center": v(-42.62, -113.38) * mm, "radius": 1.88 * mm});
            skCircle(sketch, "E2.12.26.0", {"center": v(-42.62, -125.38) * mm, "radius": 1.88 * mm});
            skCircle(sketch, "E2.12.27.0", {"center": v(-42.62, -137.38) * mm, "radius": 1.88 * mm});
            skCircle(sketch, "E2.12.28.0", {"center": v(-42.62, -149.38) * mm, "radius": 1.88 * mm});
            skCircle(sketch, "E2.12.29.0", {"center": v(-42.62, -161.38) * mm, "radius": 1.88 * mm});
            skCircle(sketch, "E2.12.30.0", {"center": v(-42.62, -173.38) * mm, "radius": 1.88 * mm});
            skCircle(sketch, "E2.12.31.0", {"center": v(-42.62, -185.38) * mm, "radius": 1.88 * mm});
            skCircle(sketch, "E2.13.0.0", {"center": v(-30.62, 186.62) * mm, "radius": 1.88 * mm});
            skCircle(sketch, "E2.13.1.0", {"center": v(-30.62, 174.62) * mm, "radius": 1.88 * mm});
            skCircle(sketch, "E2.13.2.0", {"center": v(-30.62, 162.62) * mm, "radius": 1.88 * mm});
            skCircle(sketch, "E2.13.3.0", {"center": v(-30.62, 150.62) * mm, "radius": 1.88 * mm});
            skCircle(sketch, "E2.13.4.0", {"center": v(-30.62, 138.62) * mm, "radius": 1.88 * mm});
            skCircle(sketch, "E2.13.5.0", {"center": v(-30.62, 126.62) * mm, "radius": 1.88 * mm});
            skCircle(sketch, "E2.13.6.0", {"center": v(-30.62, 114.62) * mm, "radius": 1.88 * mm});
            skCircle(sketch, "E2.13.7.0", {"center": v(-30.62, 102.62) * mm, "radius": 1.88 * mm});
            skCircle(sketch, "E2.13.8.0", {"center": v(-30.62, 90.62) * mm, "radius": 1.88 * mm});
            skCircle(sketch, "E2.13.9.0", {"center": v(-30.62, 78.62) * mm, "radius": 1.88 * mm});
            skCircle(sketch, "E2.13.10.0", {"center": v(-30.62, 66.62) * mm, "radius": 1.88 * mm});
            skCircle(sketch, "E2.13.11.0", {"center": v(-30.62, 54.62) * mm, "radius": 1.88 * mm});
            skCircle(sketch, "E2.13.12.0", {"center": v(-30.62, 42.62) * mm, "radius": 1.88 * mm});
            skCircle(sketch, "E2.13.13.0", {"center": v(-30.62, 30.62) * mm, "radius": 1.88 * mm});
            skCircle(sketch, "E2.13.14.0", {"center": v(-30.62, 18.62) * mm, "radius": 1.88 * mm});
            skCircle(sketch, "E2.13.15.0", {"center": v(-30.62, 6.62) * mm, "radius": 1.88 * mm});
            skCircle(sketch, "E2.13.16.0", {"center": v(-30.62, -5.38) * mm, "radius": 1.88 * mm});
            skCircle(sketch, "E2.13.17.0", {"center": v(-30.62, -17.38) * mm, "radius": 1.88 * mm});
            skCircle(sketch, "E2.13.18.0", {"center": v(-30.62, -29.38) * mm, "radius": 1.88 * mm});
            skCircle(sketch, "E2.13.19.0", {"center": v(-30.62, -41.38) * mm, "radius": 1.88 * mm});
            skCircle(sketch, "E2.13.20.0", {"center": v(-30.62, -53.38) * mm, "radius": 1.88 * mm});
            skCircle(sketch, "E2.13.21.0", {"center": v(-30.62, -65.38) * mm, "radius": 1.88 * mm});
            skCircle(sketch, "E2.13.22.0", {"center": v(-30.62, -77.38) * mm, "radius": 1.88 * mm});
            skCircle(sketch, "E2.13.23.0", {"center": v(-30.62, -89.38) * mm, "radius": 1.88 * mm});
            skCircle(sketch, "E2.13.24.0", {"center": v(-30.62, -101.38) * mm, "radius": 1.88 * mm});
            skCircle(sketch, "E2.13.25.0", {"center": v(-30.62, -113.38) * mm, "radius": 1.88 * mm});
            skCircle(sketch, "E2.13.26.0", {"center": v(-30.62, -125.38) * mm, "radius": 1.88 * mm});
            skCircle(sketch, "E2.13.27.0", {"center": v(-30.62, -137.38) * mm, "radius": 1.88 * mm});
            skCircle(sketch, "E2.13.28.0", {"center": v(-30.62, -149.38) * mm, "radius": 1.88 * mm});
            skCircle(sketch, "E2.13.29.0", {"center": v(-30.62, -161.38) * mm, "radius": 1.88 * mm});
            skCircle(sketch, "E2.13.30.0", {"center": v(-30.62, -173.38) * mm, "radius": 1.88 * mm});
            skCircle(sketch, "E2.13.31.0", {"center": v(-30.62, -185.38) * mm, "radius": 1.88 * mm});
            skCircle(sketch, "E2.14.0.0", {"center": v(-18.62, 186.62) * mm, "radius": 1.88 * mm});
            skCircle(sketch, "E2.14.1.0", {"center": v(-18.62, 174.62) * mm, "radius": 1.88 * mm});
            skCircle(sketch, "E2.14.2.0", {"center": v(-18.62, 162.62) * mm, "radius": 1.88 * mm});
            skCircle(sketch, "E2.14.3.0", {"center": v(-18.62, 150.62) * mm, "radius": 1.88 * mm});
            skCircle(sketch, "E2.14.4.0", {"center": v(-18.62, 138.62) * mm, "radius": 1.88 * mm});
            skCircle(sketch, "E2.14.5.0", {"center": v(-18.62, 126.62) * mm, "radius": 1.88 * mm});
            skCircle(sketch, "E2.14.6.0", {"center": v(-18.62, 114.62) * mm, "radius": 1.88 * mm});
            skCircle(sketch, "E2.14.7.0", {"center": v(-18.62, 102.62) * mm, "radius": 1.88 * mm});
            skCircle(sketch, "E2.14.8.0", {"center": v(-18.62, 90.62) * mm, "radius": 1.88 * mm});
            skCircle(sketch, "E2.14.9.0", {"center": v(-18.62, 78.62) * mm, "radius": 1.88 * mm});
            skCircle(sketch, "E2.14.10.0", {"center": v(-18.62, 66.62) * mm, "radius": 1.88 * mm});
            skCircle(sketch, "E2.14.11.0", {"center": v(-18.62, 54.62) * mm, "radius": 1.88 * mm});
            skCircle(sketch, "E2.14.12.0", {"center": v(-18.62, 42.62) * mm, "radius": 1.88 * mm});
            skCircle(sketch, "E2.14.13.0", {"center": v(-18.62, 30.62) * mm, "radius": 1.88 * mm});
            skCircle(sketch, "E2.14.14.0", {"center": v(-18.62, 18.62) * mm, "radius": 1.88 * mm});
            skCircle(sketch, "E2.14.15.0", {"center": v(-18.62, 6.62) * mm, "radius": 1.88 * mm});
            skCircle(sketch, "E2.14.16.0", {"center": v(-18.62, -5.38) * mm, "radius": 1.88 * mm});
            skCircle(sketch, "E2.14.17.0", {"center": v(-18.62, -17.38) * mm, "radius": 1.88 * mm});
            skCircle(sketch, "E2.14.18.0", {"center": v(-18.62, -29.38) * mm, "radius": 1.88 * mm});
            skCircle(sketch, "E2.14.19.0", {"center": v(-18.62, -41.38) * mm, "radius": 1.88 * mm});
            skCircle(sketch, "E2.14.20.0", {"center": v(-18.62, -53.38) * mm, "radius": 1.88 * mm});
            skCircle(sketch, "E2.14.21.0", {"center": v(-18.62, -65.38) * mm, "radius": 1.88 * mm});
            skCircle(sketch, "E2.14.22.0", {"center": v(-18.62, -77.38) * mm, "radius": 1.88 * mm});
            skCircle(sketch, "E2.14.23.0", {"center": v(-18.62, -89.38) * mm, "radius": 1.88 * mm});
            skCircle(sketch, "E2.14.24.0", {"center": v(-18.62, -101.38) * mm, "radius": 1.88 * mm});
            skCircle(sketch, "E2.14.25.0", {"center": v(-18.62, -113.38) * mm, "radius": 1.88 * mm});
            skCircle(sketch, "E2.14.26.0", {"center": v(-18.62, -125.38) * mm, "radius": 1.88 * mm});
            skCircle(sketch, "E2.14.27.0", {"center": v(-18.62, -137.38) * mm, "radius": 1.88 * mm});
            skCircle(sketch, "E2.14.28.0", {"center": v(-18.62, -149.38) * mm, "radius": 1.88 * mm});
            skCircle(sketch, "E2.14.29.0", {"center": v(-18.62, -161.38) * mm, "radius": 1.88 * mm});
            skCircle(sketch, "E2.14.30.0", {"center": v(-18.62, -173.38) * mm, "radius": 1.88 * mm});
            skCircle(sketch, "E2.14.31.0", {"center": v(-18.62, -185.38) * mm, "radius": 1.88 * mm});
            skCircle(sketch, "E2.15.0.0", {"center": v(-6.62, 186.62) * mm, "radius": 1.88 * mm});
            skCircle(sketch, "E2.15.1.0", {"center": v(-6.62, 174.62) * mm, "radius": 1.88 * mm});
            skCircle(sketch, "E2.15.2.0", {"center": v(-6.62, 162.62) * mm, "radius": 1.88 * mm});
            skCircle(sketch, "E2.15.3.0", {"center": v(-6.62, 150.62) * mm, "radius": 1.88 * mm});
            skCircle(sketch, "E2.15.4.0", {"center": v(-6.62, 138.62) * mm, "radius": 1.88 * mm});
            skCircle(sketch, "E2.15.5.0", {"center": v(-6.62, 126.62) * mm, "radius": 1.88 * mm});
            skCircle(sketch, "E2.15.6.0", {"center": v(-6.62, 114.62) * mm, "radius": 1.88 * mm});
            skCircle(sketch, "E2.15.7.0", {"center": v(-6.62, 102.62) * mm, "radius": 1.88 * mm});
            skCircle(sketch, "E2.15.8.0", {"center": v(-6.62, 90.62) * mm, "radius": 1.88 * mm});
            skCircle(sketch, "E2.15.9.0", {"center": v(-6.62, 78.62) * mm, "radius": 1.88 * mm});
            skCircle(sketch, "E2.15.10.0", {"center": v(-6.62, 66.62) * mm, "radius": 1.88 * mm});
            skCircle(sketch, "E2.15.11.0", {"center": v(-6.62, 54.62) * mm, "radius": 1.88 * mm});
            skCircle(sketch, "E2.15.12.0", {"center": v(-6.62, 42.62) * mm, "radius": 1.88 * mm});
            skCircle(sketch, "E2.15.13.0", {"center": v(-6.62, 30.62) * mm, "radius": 1.88 * mm});
            skCircle(sketch, "E2.15.14.0", {"center": v(-6.62, 18.62) * mm, "radius": 1.88 * mm});
            skCircle(sketch, "E2.15.15.0", {"center": v(-6.62, 6.62) * mm, "radius": 1.88 * mm});
            skCircle(sketch, "E2.15.16.0", {"center": v(-6.62, -5.38) * mm, "radius": 1.88 * mm});
            skCircle(sketch, "E2.15.17.0", {"center": v(-6.62, -17.38) * mm, "radius": 1.88 * mm});
            skCircle(sketch, "E2.15.18.0", {"center": v(-6.62, -29.38) * mm, "radius": 1.88 * mm});
            skCircle(sketch, "E2.15.19.0", {"center": v(-6.62, -41.38) * mm, "radius": 1.88 * mm});
            skCircle(sketch, "E2.15.20.0", {"center": v(-6.62, -53.38) * mm, "radius": 1.88 * mm});
            skCircle(sketch, "E2.15.21.0", {"center": v(-6.62, -65.38) * mm, "radius": 1.88 * mm});
            skCircle(sketch, "E2.15.22.0", {"center": v(-6.62, -77.38) * mm, "radius": 1.88 * mm});
            skCircle(sketch, "E2.15.23.0", {"center": v(-6.62, -89.38) * mm, "radius": 1.88 * mm});
            skCircle(sketch, "E2.15.24.0", {"center": v(-6.62, -101.38) * mm, "radius": 1.88 * mm});
            skCircle(sketch, "E2.15.25.0", {"center": v(-6.62, -113.38) * mm, "radius": 1.88 * mm});
            skCircle(sketch, "E2.15.26.0", {"center": v(-6.62, -125.38) * mm, "radius": 1.88 * mm});
            skCircle(sketch, "E2.15.27.0", {"center": v(-6.62, -137.38) * mm, "radius": 1.88 * mm});
            skCircle(sketch, "E2.15.28.0", {"center": v(-6.62, -149.38) * mm, "radius": 1.88 * mm});
            skCircle(sketch, "E2.15.29.0", {"center": v(-6.62, -161.38) * mm, "radius": 1.88 * mm});
            skCircle(sketch, "E2.15.30.0", {"center": v(-6.62, -173.38) * mm, "radius": 1.88 * mm});
            skCircle(sketch, "E2.15.31.0", {"center": v(-6.62, -185.38) * mm, "radius": 1.88 * mm});
            skCircle(sketch, "E2.16.0.0", {"center": v(5.38, 186.62) * mm, "radius": 1.88 * mm});
            skCircle(sketch, "E2.16.1.0", {"center": v(5.38, 174.62) * mm, "radius": 1.88 * mm});
            skCircle(sketch, "E2.16.2.0", {"center": v(5.38, 162.62) * mm, "radius": 1.88 * mm});
            skCircle(sketch, "E2.16.3.0", {"center": v(5.38, 150.62) * mm, "radius": 1.88 * mm});
            skCircle(sketch, "E2.16.4.0", {"center": v(5.38, 138.62) * mm, "radius": 1.88 * mm});
            skCircle(sketch, "E2.16.5.0", {"center": v(5.38, 126.62) * mm, "radius": 1.88 * mm});
            skCircle(sketch, "E2.16.6.0", {"center": v(5.38, 114.62) * mm, "radius": 1.88 * mm});
            skCircle(sketch, "E2.16.7.0", {"center": v(5.38, 102.62) * mm, "radius": 1.88 * mm});
            skCircle(sketch, "E2.16.8.0", {"center": v(5.38, 90.62) * mm, "radius": 1.88 * mm});
            skCircle(sketch, "E2.16.9.0", {"center": v(5.38, 78.62) * mm, "radius": 1.88 * mm});
            skCircle(sketch, "E2.16.10.0", {"center": v(5.38, 66.62) * mm, "radius": 1.88 * mm});
            skCircle(sketch, "E2.16.11.0", {"center": v(5.38, 54.62) * mm, "radius": 1.88 * mm});
            skCircle(sketch, "E2.16.12.0", {"center": v(5.38, 42.62) * mm, "radius": 1.88 * mm});
            skCircle(sketch, "E2.16.13.0", {"center": v(5.38, 30.62) * mm, "radius": 1.88 * mm});
            skCircle(sketch, "E2.16.14.0", {"center": v(5.38, 18.62) * mm, "radius": 1.88 * mm});
            skCircle(sketch, "E2.16.15.0", {"center": v(5.38, 6.62) * mm, "radius": 1.88 * mm});
            skCircle(sketch, "E2.16.16.0", {"center": v(5.38, -5.38) * mm, "radius": 1.88 * mm});
            skCircle(sketch, "E2.16.17.0", {"center": v(5.38, -17.38) * mm, "radius": 1.88 * mm});
            skCircle(sketch, "E2.16.18.0", {"center": v(5.38, -29.38) * mm, "radius": 1.88 * mm});
            skCircle(sketch, "E2.16.19.0", {"center": v(5.38, -41.38) * mm, "radius": 1.88 * mm});
            skCircle(sketch, "E2.16.20.0", {"center": v(5.38, -53.38) * mm, "radius": 1.88 * mm});
            skCircle(sketch, "E2.16.21.0", {"center": v(5.38, -65.38) * mm, "radius": 1.88 * mm});
            skCircle(sketch, "E2.16.22.0", {"center": v(5.38, -77.38) * mm, "radius": 1.88 * mm});
            skCircle(sketch, "E2.16.23.0", {"center": v(5.38, -89.38) * mm, "radius": 1.88 * mm});
            skCircle(sketch, "E2.16.24.0", {"center": v(5.38, -101.38) * mm, "radius": 1.88 * mm});
            skCircle(sketch, "E2.16.25.0", {"center": v(5.38, -113.38) * mm, "radius": 1.88 * mm});
            skCircle(sketch, "E2.16.26.0", {"center": v(5.38, -125.38) * mm, "radius": 1.88 * mm});
            skCircle(sketch, "E2.16.27.0", {"center": v(5.38, -137.38) * mm, "radius": 1.88 * mm});
            skCircle(sketch, "E2.16.28.0", {"center": v(5.38, -149.38) * mm, "radius": 1.88 * mm});
            skCircle(sketch, "E2.16.29.0", {"center": v(5.38, -161.38) * mm, "radius": 1.88 * mm});
            skCircle(sketch, "E2.16.30.0", {"center": v(5.38, -173.38) * mm, "radius": 1.88 * mm});
            skCircle(sketch, "E2.16.31.0", {"center": v(5.38, -185.38) * mm, "radius": 1.88 * mm});
            skCircle(sketch, "E2.17.0.0", {"center": v(17.38, 186.62) * mm, "radius": 1.88 * mm});
            skCircle(sketch, "E2.17.1.0", {"center": v(17.38, 174.62) * mm, "radius": 1.88 * mm});
            skCircle(sketch, "E2.17.2.0", {"center": v(17.38, 162.62) * mm, "radius": 1.88 * mm});
            skCircle(sketch, "E2.17.3.0", {"center": v(17.38, 150.62) * mm, "radius": 1.88 * mm});
            skCircle(sketch, "E2.17.4.0", {"center": v(17.38, 138.62) * mm, "radius": 1.88 * mm});
            skCircle(sketch, "E2.17.5.0", {"center": v(17.38, 126.62) * mm, "radius": 1.88 * mm});
            skCircle(sketch, "E2.17.6.0", {"center": v(17.38, 114.62) * mm, "radius": 1.88 * mm});
            skCircle(sketch, "E2.17.7.0", {"center": v(17.38, 102.62) * mm, "radius": 1.88 * mm});
            skCircle(sketch, "E2.17.8.0", {"center": v(17.38, 90.62) * mm, "radius": 1.88 * mm});
            skCircle(sketch, "E2.17.9.0", {"center": v(17.38, 78.62) * mm, "radius": 1.88 * mm});
            skCircle(sketch, "E2.17.10.0", {"center": v(17.38, 66.62) * mm, "radius": 1.88 * mm});
            skCircle(sketch, "E2.17.11.0", {"center": v(17.38, 54.62) * mm, "radius": 1.88 * mm});
            skCircle(sketch, "E2.17.12.0", {"center": v(17.38, 42.62) * mm, "radius": 1.88 * mm});
            skCircle(sketch, "E2.17.13.0", {"center": v(17.38, 30.62) * mm, "radius": 1.88 * mm});
            skCircle(sketch, "E2.17.14.0", {"center": v(17.38, 18.62) * mm, "radius": 1.88 * mm});
            skCircle(sketch, "E2.17.15.0", {"center": v(17.38, 6.62) * mm, "radius": 1.88 * mm});
            skCircle(sketch, "E2.17.16.0", {"center": v(17.38, -5.38) * mm, "radius": 1.88 * mm});
            skCircle(sketch, "E2.17.17.0", {"center": v(17.38, -17.38) * mm, "radius": 1.88 * mm});
            skCircle(sketch, "E2.17.18.0", {"center": v(17.38, -29.38) * mm, "radius": 1.88 * mm});
            skCircle(sketch, "E2.17.19.0", {"center": v(17.38, -41.38) * mm, "radius": 1.88 * mm});
            skCircle(sketch, "E2.17.20.0", {"center": v(17.38, -53.38) * mm, "radius": 1.88 * mm});
            skCircle(sketch, "E2.17.21.0", {"center": v(17.38, -65.38) * mm, "radius": 1.88 * mm});
            skCircle(sketch, "E2.17.22.0", {"center": v(17.38, -77.38) * mm, "radius": 1.88 * mm});
            skCircle(sketch, "E2.17.23.0", {"center": v(17.38, -89.38) * mm, "radius": 1.88 * mm});
            skCircle(sketch, "E2.17.24.0", {"center": v(17.38, -101.38) * mm, "radius": 1.88 * mm});
            skCircle(sketch, "E2.17.25.0", {"center": v(17.38, -113.38) * mm, "radius": 1.88 * mm});
            skCircle(sketch, "E2.17.26.0", {"center": v(17.38, -125.38) * mm, "radius": 1.88 * mm});
            skCircle(sketch, "E2.17.27.0", {"center": v(17.38, -137.38) * mm, "radius": 1.88 * mm});
            skCircle(sketch, "E2.17.28.0", {"center": v(17.38, -149.38) * mm, "radius": 1.88 * mm});
            skCircle(sketch, "E2.17.29.0", {"center": v(17.38, -161.38) * mm, "radius": 1.88 * mm});
            skCircle(sketch, "E2.17.30.0", {"center": v(17.38, -173.38) * mm, "radius": 1.88 * mm});
            skCircle(sketch, "E2.17.31.0", {"center": v(17.38, -185.38) * mm, "radius": 1.88 * mm});
            skCircle(sketch, "E2.18.0.0", {"center": v(29.38, 186.62) * mm, "radius": 1.88 * mm});
            skCircle(sketch, "E2.18.1.0", {"center": v(29.38, 174.62) * mm, "radius": 1.88 * mm});
            skCircle(sketch, "E2.18.2.0", {"center": v(29.38, 162.62) * mm, "radius": 1.88 * mm});
            skCircle(sketch, "E2.18.3.0", {"center": v(29.38, 150.62) * mm, "radius": 1.88 * mm});
            skCircle(sketch, "E2.18.4.0", {"center": v(29.38, 138.62) * mm, "radius": 1.88 * mm});
            skCircle(sketch, "E2.18.5.0", {"center": v(29.38, 126.62) * mm, "radius": 1.88 * mm});
            skCircle(sketch, "E2.18.6.0", {"center": v(29.38, 114.62) * mm, "radius": 1.88 * mm});
            skCircle(sketch, "E2.18.7.0", {"center": v(29.38, 102.62) * mm, "radius": 1.88 * mm});
            skCircle(sketch, "E2.18.8.0", {"center": v(29.38, 90.62) * mm, "radius": 1.88 * mm});
            skCircle(sketch, "E2.18.9.0", {"center": v(29.38, 78.62) * mm, "radius": 1.88 * mm});
            skCircle(sketch, "E2.18.10.0", {"center": v(29.38, 66.62) * mm, "radius": 1.88 * mm});
            skCircle(sketch, "E2.18.11.0", {"center": v(29.38, 54.62) * mm, "radius": 1.88 * mm});
            skCircle(sketch, "E2.18.12.0", {"center": v(29.38, 42.62) * mm, "radius": 1.88 * mm});
            skCircle(sketch, "E2.18.13.0", {"center": v(29.38, 30.62) * mm, "radius": 1.88 * mm});
            skCircle(sketch, "E2.18.14.0", {"center": v(29.38, 18.62) * mm, "radius": 1.88 * mm});
            skCircle(sketch, "E2.18.15.0", {"center": v(29.38, 6.62) * mm, "radius": 1.88 * mm});
            skCircle(sketch, "E2.18.16.0", {"center": v(29.38, -5.38) * mm, "radius": 1.88 * mm});
            skCircle(sketch, "E2.18.17.0", {"center": v(29.38, -17.38) * mm, "radius": 1.88 * mm});
            skCircle(sketch, "E2.18.18.0", {"center": v(29.38, -29.38) * mm, "radius": 1.88 * mm});
            skCircle(sketch, "E2.18.19.0", {"center": v(29.38, -41.38) * mm, "radius": 1.88 * mm});
            skCircle(sketch, "E2.18.20.0", {"center": v(29.38, -53.38) * mm, "radius": 1.88 * mm});
            skCircle(sketch, "E2.18.21.0", {"center": v(29.38, -65.38) * mm, "radius": 1.88 * mm});
            skCircle(sketch, "E2.18.22.0", {"center": v(29.38, -77.38) * mm, "radius": 1.88 * mm});
            skCircle(sketch, "E2.18.23.0", {"center": v(29.38, -89.38) * mm, "radius": 1.88 * mm});
            skCircle(sketch, "E2.18.24.0", {"center": v(29.38, -101.38) * mm, "radius": 1.88 * mm});
            skCircle(sketch, "E2.18.25.0", {"center": v(29.38, -113.38) * mm, "radius": 1.88 * mm});
            skCircle(sketch, "E2.18.26.0", {"center": v(29.38, -125.38) * mm, "radius": 1.88 * mm});
            skCircle(sketch, "E2.18.27.0", {"center": v(29.38, -137.38) * mm, "radius": 1.88 * mm});
            skCircle(sketch, "E2.18.28.0", {"center": v(29.38, -149.38) * mm, "radius": 1.88 * mm});
            skCircle(sketch, "E2.18.29.0", {"center": v(29.38, -161.38) * mm, "radius": 1.88 * mm});
            skCircle(sketch, "E2.18.30.0", {"center": v(29.38, -173.38) * mm, "radius": 1.88 * mm});
            skCircle(sketch, "E2.18.31.0", {"center": v(29.38, -185.38) * mm, "radius": 1.88 * mm});
            skCircle(sketch, "E2.19.0.0", {"center": v(41.38, 186.62) * mm, "radius": 1.88 * mm});
            skCircle(sketch, "E2.19.1.0", {"center": v(41.38, 174.62) * mm, "radius": 1.88 * mm});
            skCircle(sketch, "E2.19.2.0", {"center": v(41.38, 162.62) * mm, "radius": 1.88 * mm});
            skCircle(sketch, "E2.19.3.0", {"center": v(41.38, 150.62) * mm, "radius": 1.88 * mm});
            skCircle(sketch, "E2.19.4.0", {"center": v(41.38, 138.62) * mm, "radius": 1.88 * mm});
            skCircle(sketch, "E2.19.5.0", {"center": v(41.38, 126.62) * mm, "radius": 1.88 * mm});
            skCircle(sketch, "E2.19.6.0", {"center": v(41.38, 114.62) * mm, "radius": 1.88 * mm});
            skCircle(sketch, "E2.19.7.0", {"center": v(41.38, 102.62) * mm, "radius": 1.88 * mm});
            skCircle(sketch, "E2.19.8.0", {"center": v(41.38, 90.62) * mm, "radius": 1.88 * mm});
            skCircle(sketch, "E2.19.9.0", {"center": v(41.38, 78.62) * mm, "radius": 1.88 * mm});
            skCircle(sketch, "E2.19.10.0", {"center": v(41.38, 66.62) * mm, "radius": 1.88 * mm});
            skCircle(sketch, "E2.19.11.0", {"center": v(41.38, 54.62) * mm, "radius": 1.88 * mm});
            skCircle(sketch, "E2.19.12.0", {"center": v(41.38, 42.62) * mm, "radius": 1.88 * mm});
            skCircle(sketch, "E2.19.13.0", {"center": v(41.38, 30.62) * mm, "radius": 1.88 * mm});
            skCircle(sketch, "E2.19.14.0", {"center": v(41.38, 18.62) * mm, "radius": 1.88 * mm});
            skCircle(sketch, "E2.19.15.0", {"center": v(41.38, 6.62) * mm, "radius": 1.88 * mm});
            skCircle(sketch, "E2.19.16.0", {"center": v(41.38, -5.38) * mm, "radius": 1.88 * mm});
            skCircle(sketch, "E2.19.17.0", {"center": v(41.38, -17.38) * mm, "radius": 1.88 * mm});
            skCircle(sketch, "E2.19.18.0", {"center": v(41.38, -29.38) * mm, "radius": 1.88 * mm});
            skCircle(sketch, "E2.19.19.0", {"center": v(41.38, -41.38) * mm, "radius": 1.88 * mm});
            skCircle(sketch, "E2.19.20.0", {"center": v(41.38, -53.38) * mm, "radius": 1.88 * mm});
            skCircle(sketch, "E2.19.21.0", {"center": v(41.38, -65.38) * mm, "radius": 1.88 * mm});
            skCircle(sketch, "E2.19.22.0", {"center": v(41.38, -77.38) * mm, "radius": 1.88 * mm});
            skCircle(sketch, "E2.19.23.0", {"center": v(41.38, -89.38) * mm, "radius": 1.88 * mm});
            skCircle(sketch, "E2.19.24.0", {"center": v(41.38, -101.38) * mm, "radius": 1.88 * mm});
            skCircle(sketch, "E2.19.25.0", {"center": v(41.38, -113.38) * mm, "radius": 1.88 * mm});
            skCircle(sketch, "E2.19.26.0", {"center": v(41.38, -125.38) * mm, "radius": 1.88 * mm});
            skCircle(sketch, "E2.19.27.0", {"center": v(41.38, -137.38) * mm, "radius": 1.88 * mm});
            skCircle(sketch, "E2.19.28.0", {"center": v(41.38, -149.38) * mm, "radius": 1.88 * mm});
            skCircle(sketch, "E2.19.29.0", {"center": v(41.38, -161.38) * mm, "radius": 1.88 * mm});
            skCircle(sketch, "E2.19.30.0", {"center": v(41.38, -173.38) * mm, "radius": 1.88 * mm});
            skCircle(sketch, "E2.19.31.0", {"center": v(41.38, -185.38) * mm, "radius": 1.88 * mm});
            skCircle(sketch, "E2.20.0.0", {"center": v(53.38, 186.62) * mm, "radius": 1.88 * mm});
            skCircle(sketch, "E2.20.1.0", {"center": v(53.38, 174.62) * mm, "radius": 1.88 * mm});
            skCircle(sketch, "E2.20.2.0", {"center": v(53.38, 162.62) * mm, "radius": 1.88 * mm});
            skCircle(sketch, "E2.20.3.0", {"center": v(53.38, 150.62) * mm, "radius": 1.88 * mm});
            skCircle(sketch, "E2.20.4.0", {"center": v(53.38, 138.62) * mm, "radius": 1.88 * mm});
            skCircle(sketch, "E2.20.5.0", {"center": v(53.38, 126.62) * mm, "radius": 1.88 * mm});
            skCircle(sketch, "E2.20.6.0", {"center": v(53.38, 114.62) * mm, "radius": 1.88 * mm});
            skCircle(sketch, "E2.20.7.0", {"center": v(53.38, 102.62) * mm, "radius": 1.88 * mm});
            skCircle(sketch, "E2.20.8.0", {"center": v(53.38, 90.62) * mm, "radius": 1.88 * mm});
            skCircle(sketch, "E2.20.9.0", {"center": v(53.38, 78.62) * mm, "radius": 1.88 * mm});
            skCircle(sketch, "E2.20.10.0", {"center": v(53.38, 66.62) * mm, "radius": 1.88 * mm});
            skCircle(sketch, "E2.20.11.0", {"center": v(53.38, 54.62) * mm, "radius": 1.88 * mm});
            skCircle(sketch, "E2.20.12.0", {"center": v(53.38, 42.62) * mm, "radius": 1.88 * mm});
            skCircle(sketch, "E2.20.13.0", {"center": v(53.38, 30.62) * mm, "radius": 1.88 * mm});
            skCircle(sketch, "E2.20.14.0", {"center": v(53.38, 18.62) * mm, "radius": 1.88 * mm});
            skCircle(sketch, "E2.20.15.0", {"center": v(53.38, 6.62) * mm, "radius": 1.88 * mm});
            skCircle(sketch, "E2.20.16.0", {"center": v(53.38, -5.38) * mm, "radius": 1.88 * mm});
            skCircle(sketch, "E2.20.17.0", {"center": v(53.38, -17.38) * mm, "radius": 1.88 * mm});
            skCircle(sketch, "E2.20.18.0", {"center": v(53.38, -29.38) * mm, "radius": 1.88 * mm});
            skCircle(sketch, "E2.20.19.0", {"center": v(53.38, -41.38) * mm, "radius": 1.88 * mm});
            skCircle(sketch, "E2.20.20.0", {"center": v(53.38, -53.38) * mm, "radius": 1.88 * mm});
            skCircle(sketch, "E2.20.21.0", {"center": v(53.38, -65.38) * mm, "radius": 1.88 * mm});
            skCircle(sketch, "E2.20.22.0", {"center": v(53.38, -77.38) * mm, "radius": 1.88 * mm});
            skCircle(sketch, "E2.20.23.0", {"center": v(53.38, -89.38) * mm, "radius": 1.88 * mm});
            skCircle(sketch, "E2.20.24.0", {"center": v(53.38, -101.38) * mm, "radius": 1.88 * mm});
            skCircle(sketch, "E2.20.25.0", {"center": v(53.38, -113.38) * mm, "radius": 1.88 * mm});
            skCircle(sketch, "E2.20.26.0", {"center": v(53.38, -125.38) * mm, "radius": 1.88 * mm});
            skCircle(sketch, "E2.20.27.0", {"center": v(53.38, -137.38) * mm, "radius": 1.88 * mm});
            skCircle(sketch, "E2.20.28.0", {"center": v(53.38, -149.38) * mm, "radius": 1.88 * mm});
            skCircle(sketch, "E2.20.29.0", {"center": v(53.38, -161.38) * mm, "radius": 1.88 * mm});
            skCircle(sketch, "E2.20.30.0", {"center": v(53.38, -173.38) * mm, "radius": 1.88 * mm});
            skCircle(sketch, "E2.20.31.0", {"center": v(53.38, -185.38) * mm, "radius": 1.88 * mm});
            skCircle(sketch, "E2.21.0.0", {"center": v(65.38, 186.62) * mm, "radius": 1.88 * mm});
            skCircle(sketch, "E2.21.1.0", {"center": v(65.38, 174.62) * mm, "radius": 1.88 * mm});
            skCircle(sketch, "E2.21.2.0", {"center": v(65.38, 162.62) * mm, "radius": 1.88 * mm});
            skCircle(sketch, "E2.21.3.0", {"center": v(65.38, 150.62) * mm, "radius": 1.88 * mm});
            skCircle(sketch, "E2.21.4.0", {"center": v(65.38, 138.62) * mm, "radius": 1.88 * mm});
            skCircle(sketch, "E2.21.5.0", {"center": v(65.38, 126.62) * mm, "radius": 1.88 * mm});
            skCircle(sketch, "E2.21.6.0", {"center": v(65.38, 114.62) * mm, "radius": 1.88 * mm});
            skCircle(sketch, "E2.21.7.0", {"center": v(65.38, 102.62) * mm, "radius": 1.88 * mm});
            skCircle(sketch, "E2.21.8.0", {"center": v(65.38, 90.62) * mm, "radius": 1.88 * mm});
            skCircle(sketch, "E2.21.9.0", {"center": v(65.38, 78.62) * mm, "radius": 1.88 * mm});
            skCircle(sketch, "E2.21.10.0", {"center": v(65.38, 66.62) * mm, "radius": 1.88 * mm});
            skCircle(sketch, "E2.21.11.0", {"center": v(65.38, 54.62) * mm, "radius": 1.88 * mm});
            skCircle(sketch, "E2.21.12.0", {"center": v(65.38, 42.62) * mm, "radius": 1.88 * mm});
            skCircle(sketch, "E2.21.13.0", {"center": v(65.38, 30.62) * mm, "radius": 1.88 * mm});
            skCircle(sketch, "E2.21.14.0", {"center": v(65.38, 18.62) * mm, "radius": 1.88 * mm});
            skCircle(sketch, "E2.21.15.0", {"center": v(65.38, 6.62) * mm, "radius": 1.88 * mm});
            skCircle(sketch, "E2.21.16.0", {"center": v(65.38, -5.38) * mm, "radius": 1.88 * mm});
            skCircle(sketch, "E2.21.17.0", {"center": v(65.38, -17.38) * mm, "radius": 1.88 * mm});
            skCircle(sketch, "E2.21.18.0", {"center": v(65.38, -29.38) * mm, "radius": 1.88 * mm});
            skCircle(sketch, "E2.21.19.0", {"center": v(65.38, -41.38) * mm, "radius": 1.88 * mm});
            skCircle(sketch, "E2.21.20.0", {"center": v(65.38, -53.38) * mm, "radius": 1.88 * mm});
            skCircle(sketch, "E2.21.21.0", {"center": v(65.38, -65.38) * mm, "radius": 1.88 * mm});
            skCircle(sketch, "E2.21.22.0", {"center": v(65.38, -77.38) * mm, "radius": 1.88 * mm});
            skCircle(sketch, "E2.21.23.0", {"center": v(65.38, -89.38) * mm, "radius": 1.88 * mm});
            skCircle(sketch, "E2.21.24.0", {"center": v(65.38, -101.38) * mm, "radius": 1.88 * mm});
            skCircle(sketch, "E2.21.25.0", {"center": v(65.38, -113.38) * mm, "radius": 1.88 * mm});
            skCircle(sketch, "E2.21.26.0", {"center": v(65.38, -125.38) * mm, "radius": 1.88 * mm});
            skCircle(sketch, "E2.21.27.0", {"center": v(65.38, -137.38) * mm, "radius": 1.88 * mm});
            skCircle(sketch, "E2.21.28.0", {"center": v(65.38, -149.38) * mm, "radius": 1.88 * mm});
            skCircle(sketch, "E2.21.29.0", {"center": v(65.38, -161.38) * mm, "radius": 1.88 * mm});
            skCircle(sketch, "E2.21.30.0", {"center": v(65.38, -173.38) * mm, "radius": 1.88 * mm});
            skCircle(sketch, "E2.21.31.0", {"center": v(65.38, -185.38) * mm, "radius": 1.88 * mm});
            skCircle(sketch, "E2.22.0.0", {"center": v(77.38, 186.62) * mm, "radius": 1.88 * mm});
            skCircle(sketch, "E2.22.1.0", {"center": v(77.38, 174.62) * mm, "radius": 1.88 * mm});
            skCircle(sketch, "E2.22.2.0", {"center": v(77.38, 162.62) * mm, "radius": 1.88 * mm});
            skCircle(sketch, "E2.22.3.0", {"center": v(77.38, 150.62) * mm, "radius": 1.88 * mm});
            skCircle(sketch, "E2.22.4.0", {"center": v(77.38, 138.62) * mm, "radius": 1.88 * mm});
            skCircle(sketch, "E2.22.5.0", {"center": v(77.38, 126.62) * mm, "radius": 1.88 * mm});
            skCircle(sketch, "E2.22.6.0", {"center": v(77.38, 114.62) * mm, "radius": 1.88 * mm});
            skCircle(sketch, "E2.22.7.0", {"center": v(77.38, 102.62) * mm, "radius": 1.88 * mm});
            skCircle(sketch, "E2.22.8.0", {"center": v(77.38, 90.62) * mm, "radius": 1.88 * mm});
            skCircle(sketch, "E2.22.9.0", {"center": v(77.38, 78.62) * mm, "radius": 1.88 * mm});
            skCircle(sketch, "E2.22.10.0", {"center": v(77.38, 66.62) * mm, "radius": 1.88 * mm});
            skCircle(sketch, "E2.22.11.0", {"center": v(77.38, 54.62) * mm, "radius": 1.88 * mm});
            skCircle(sketch, "E2.22.12.0", {"center": v(77.38, 42.62) * mm, "radius": 1.88 * mm});
            skCircle(sketch, "E2.22.13.0", {"center": v(77.38, 30.62) * mm, "radius": 1.88 * mm});
            skCircle(sketch, "E2.22.14.0", {"center": v(77.38, 18.62) * mm, "radius": 1.88 * mm});
            skCircle(sketch, "E2.22.15.0", {"center": v(77.38, 6.62) * mm, "radius": 1.88 * mm});
            skCircle(sketch, "E2.22.16.0", {"center": v(77.38, -5.38) * mm, "radius": 1.88 * mm});
            skCircle(sketch, "E2.22.17.0", {"center": v(77.38, -17.38) * mm, "radius": 1.88 * mm});
            skCircle(sketch, "E2.22.18.0", {"center": v(77.38, -29.38) * mm, "radius": 1.88 * mm});
            skCircle(sketch, "E2.22.19.0", {"center": v(77.38, -41.38) * mm, "radius": 1.88 * mm});
            skCircle(sketch, "E2.22.20.0", {"center": v(77.38, -53.38) * mm, "radius": 1.88 * mm});
            skCircle(sketch, "E2.22.21.0", {"center": v(77.38, -65.38) * mm, "radius": 1.88 * mm});
            skCircle(sketch, "E2.22.22.0", {"center": v(77.38, -77.38) * mm, "radius": 1.88 * mm});
            skCircle(sketch, "E2.22.23.0", {"center": v(77.38, -89.38) * mm, "radius": 1.88 * mm});
            skCircle(sketch, "E2.22.24.0", {"center": v(77.38, -101.38) * mm, "radius": 1.88 * mm});
            skCircle(sketch, "E2.22.25.0", {"center": v(77.38, -113.38) * mm, "radius": 1.88 * mm});
            skCircle(sketch, "E2.22.26.0", {"center": v(77.38, -125.38) * mm, "radius": 1.88 * mm});
            skCircle(sketch, "E2.22.27.0", {"center": v(77.38, -137.38) * mm, "radius": 1.88 * mm});
            skCircle(sketch, "E2.22.28.0", {"center": v(77.38, -149.38) * mm, "radius": 1.88 * mm});
            skCircle(sketch, "E2.22.29.0", {"center": v(77.38, -161.38) * mm, "radius": 1.88 * mm});
            skCircle(sketch, "E2.22.30.0", {"center": v(77.38, -173.38) * mm, "radius": 1.88 * mm});
            skCircle(sketch, "E2.22.31.0", {"center": v(77.38, -185.38) * mm, "radius": 1.88 * mm});
            skCircle(sketch, "E2.23.0.0", {"center": v(89.38, 186.62) * mm, "radius": 1.88 * mm});
            skCircle(sketch, "E2.23.1.0", {"center": v(89.38, 174.62) * mm, "radius": 1.88 * mm});
            skCircle(sketch, "E2.23.2.0", {"center": v(89.38, 162.62) * mm, "radius": 1.88 * mm});
            skCircle(sketch, "E2.23.3.0", {"center": v(89.38, 150.62) * mm, "radius": 1.88 * mm});
            skCircle(sketch, "E2.23.4.0", {"center": v(89.38, 138.62) * mm, "radius": 1.88 * mm});
            skCircle(sketch, "E2.23.5.0", {"center": v(89.38, 126.62) * mm, "radius": 1.88 * mm});
            skCircle(sketch, "E2.23.6.0", {"center": v(89.38, 114.62) * mm, "radius": 1.88 * mm});
            skCircle(sketch, "E2.23.7.0", {"center": v(89.38, 102.62) * mm, "radius": 1.88 * mm});
            skCircle(sketch, "E2.23.8.0", {"center": v(89.38, 90.62) * mm, "radius": 1.88 * mm});
            skCircle(sketch, "E2.23.9.0", {"center": v(89.38, 78.62) * mm, "radius": 1.88 * mm});
            skCircle(sketch, "E2.23.10.0", {"center": v(89.38, 66.62) * mm, "radius": 1.88 * mm});
            skCircle(sketch, "E2.23.11.0", {"center": v(89.38, 54.62) * mm, "radius": 1.88 * mm});
            skCircle(sketch, "E2.23.12.0", {"center": v(89.38, 42.62) * mm, "radius": 1.88 * mm});
            skCircle(sketch, "E2.23.13.0", {"center": v(89.38, 30.62) * mm, "radius": 1.88 * mm});
            skCircle(sketch, "E2.23.14.0", {"center": v(89.38, 18.62) * mm, "radius": 1.88 * mm});
            skCircle(sketch, "E2.23.15.0", {"center": v(89.38, 6.62) * mm, "radius": 1.88 * mm});
            skCircle(sketch, "E2.23.16.0", {"center": v(89.38, -5.38) * mm, "radius": 1.88 * mm});
            skCircle(sketch, "E2.23.17.0", {"center": v(89.38, -17.38) * mm, "radius": 1.88 * mm});
            skCircle(sketch, "E2.23.18.0", {"center": v(89.38, -29.38) * mm, "radius": 1.88 * mm});
            skCircle(sketch, "E2.23.19.0", {"center": v(89.38, -41.38) * mm, "radius": 1.88 * mm});
            skCircle(sketch, "E2.23.20.0", {"center": v(89.38, -53.38) * mm, "radius": 1.88 * mm});
            skCircle(sketch, "E2.23.21.0", {"center": v(89.38, -65.38) * mm, "radius": 1.88 * mm});
            skCircle(sketch, "E2.23.22.0", {"center": v(89.38, -77.38) * mm, "radius": 1.88 * mm});
            skCircle(sketch, "E2.23.23.0", {"center": v(89.38, -89.38) * mm, "radius": 1.88 * mm});
            skCircle(sketch, "E2.23.24.0", {"center": v(89.38, -101.38) * mm, "radius": 1.88 * mm});
            skCircle(sketch, "E2.23.25.0", {"center": v(89.38, -113.38) * mm, "radius": 1.88 * mm});
            skCircle(sketch, "E2.23.26.0", {"center": v(89.38, -125.38) * mm, "radius": 1.88 * mm});
            skCircle(sketch, "E2.23.27.0", {"center": v(89.38, -137.38) * mm, "radius": 1.88 * mm});
            skCircle(sketch, "E2.23.28.0", {"center": v(89.38, -149.38) * mm, "radius": 1.88 * mm});
            skCircle(sketch, "E2.23.29.0", {"center": v(89.38, -161.38) * mm, "radius": 1.88 * mm});
            skCircle(sketch, "E2.23.30.0", {"center": v(89.38, -173.38) * mm, "radius": 1.88 * mm});
            skCircle(sketch, "E2.23.31.0", {"center": v(89.38, -185.38) * mm, "radius": 1.88 * mm});
            skCircle(sketch, "E2.24.0.0", {"center": v(101.38, 186.62) * mm, "radius": 1.88 * mm});
            skCircle(sketch, "E2.24.1.0", {"center": v(101.38, 174.62) * mm, "radius": 1.88 * mm});
            skCircle(sketch, "E2.24.2.0", {"center": v(101.38, 162.62) * mm, "radius": 1.88 * mm});
            skCircle(sketch, "E2.24.3.0", {"center": v(101.38, 150.62) * mm, "radius": 1.88 * mm});
            skCircle(sketch, "E2.24.4.0", {"center": v(101.38, 138.62) * mm, "radius": 1.88 * mm});
            skCircle(sketch, "E2.24.5.0", {"center": v(101.38, 126.62) * mm, "radius": 1.88 * mm});
            skCircle(sketch, "E2.24.6.0", {"center": v(101.38, 114.62) * mm, "radius": 1.88 * mm});
            skCircle(sketch, "E2.24.7.0", {"center": v(101.38, 102.62) * mm, "radius": 1.88 * mm});
            skCircle(sketch, "E2.24.8.0", {"center": v(101.38, 90.62) * mm, "radius": 1.88 * mm});
            skCircle(sketch, "E2.24.9.0", {"center": v(101.38, 78.62) * mm, "radius": 1.88 * mm});
            skCircle(sketch, "E2.24.10.0", {"center": v(101.38, 66.62) * mm, "radius": 1.88 * mm});
            skCircle(sketch, "E2.24.11.0", {"center": v(101.38, 54.62) * mm, "radius": 1.88 * mm});
            skCircle(sketch, "E2.24.12.0", {"center": v(101.38, 42.62) * mm, "radius": 1.88 * mm});
            skCircle(sketch, "E2.24.13.0", {"center": v(101.38, 30.62) * mm, "radius": 1.88 * mm});
            skCircle(sketch, "E2.24.14.0", {"center": v(101.38, 18.62) * mm, "radius": 1.88 * mm});
            skCircle(sketch, "E2.24.15.0", {"center": v(101.38, 6.62) * mm, "radius": 1.88 * mm});
            skCircle(sketch, "E2.24.16.0", {"center": v(101.38, -5.38) * mm, "radius": 1.88 * mm});
            skCircle(sketch, "E2.24.17.0", {"center": v(101.38, -17.38) * mm, "radius": 1.88 * mm});
            skCircle(sketch, "E2.24.18.0", {"center": v(101.38, -29.38) * mm, "radius": 1.88 * mm});
            skCircle(sketch, "E2.24.19.0", {"center": v(101.38, -41.38) * mm, "radius": 1.88 * mm});
            skCircle(sketch, "E2.24.20.0", {"center": v(101.38, -53.38) * mm, "radius": 1.88 * mm});
            skCircle(sketch, "E2.24.21.0", {"center": v(101.38, -65.38) * mm, "radius": 1.88 * mm});
            skCircle(sketch, "E2.24.22.0", {"center": v(101.38, -77.38) * mm, "radius": 1.88 * mm});
            skCircle(sketch, "E2.24.23.0", {"center": v(101.38, -89.38) * mm, "radius": 1.88 * mm});
            skCircle(sketch, "E2.24.24.0", {"center": v(101.38, -101.38) * mm, "radius": 1.88 * mm});
            skCircle(sketch, "E2.24.25.0", {"center": v(101.38, -113.38) * mm, "radius": 1.88 * mm});
            skCircle(sketch, "E2.24.26.0", {"center": v(101.38, -125.38) * mm, "radius": 1.88 * mm});
            skCircle(sketch, "E2.24.27.0", {"center": v(101.38, -137.38) * mm, "radius": 1.88 * mm});
            skCircle(sketch, "E2.24.28.0", {"center": v(101.38, -149.38) * mm, "radius": 1.88 * mm});
            skCircle(sketch, "E2.24.29.0", {"center": v(101.38, -161.38) * mm, "radius": 1.88 * mm});
            skCircle(sketch, "E2.24.30.0", {"center": v(101.38, -173.38) * mm, "radius": 1.88 * mm});
            skCircle(sketch, "E2.24.31.0", {"center": v(101.38, -185.38) * mm, "radius": 1.88 * mm});
            skCircle(sketch, "E2.25.0.0", {"center": v(113.38, 186.62) * mm, "radius": 1.88 * mm});
            skCircle(sketch, "E2.25.1.0", {"center": v(113.38, 174.62) * mm, "radius": 1.88 * mm});
            skCircle(sketch, "E2.25.2.0", {"center": v(113.38, 162.62) * mm, "radius": 1.88 * mm});
            skCircle(sketch, "E2.25.3.0", {"center": v(113.38, 150.62) * mm, "radius": 1.88 * mm});
            skCircle(sketch, "E2.25.4.0", {"center": v(113.38, 138.62) * mm, "radius": 1.88 * mm});
            skCircle(sketch, "E2.25.5.0", {"center": v(113.38, 126.62) * mm, "radius": 1.88 * mm});
            skCircle(sketch, "E2.25.6.0", {"center": v(113.38, 114.62) * mm, "radius": 1.88 * mm});
            skCircle(sketch, "E2.25.7.0", {"center": v(113.38, 102.62) * mm, "radius": 1.88 * mm});
            skCircle(sketch, "E2.25.8.0", {"center": v(113.38, 90.62) * mm, "radius": 1.88 * mm});
            skCircle(sketch, "E2.25.9.0", {"center": v(113.38, 78.62) * mm, "radius": 1.88 * mm});
            skCircle(sketch, "E2.25.10.0", {"center": v(113.38, 66.62) * mm, "radius": 1.88 * mm});
            skCircle(sketch, "E2.25.11.0", {"center": v(113.38, 54.62) * mm, "radius": 1.88 * mm});
            skCircle(sketch, "E2.25.12.0", {"center": v(113.38, 42.62) * mm, "radius": 1.88 * mm});
            skCircle(sketch, "E2.25.13.0", {"center": v(113.38, 30.62) * mm, "radius": 1.88 * mm});
            skCircle(sketch, "E2.25.14.0", {"center": v(113.38, 18.62) * mm, "radius": 1.88 * mm});
            skCircle(sketch, "E2.25.15.0", {"center": v(113.38, 6.62) * mm, "radius": 1.88 * mm});
            skCircle(sketch, "E2.25.16.0", {"center": v(113.38, -5.38) * mm, "radius": 1.88 * mm});
            skCircle(sketch, "E2.25.17.0", {"center": v(113.38, -17.38) * mm, "radius": 1.88 * mm});
            skCircle(sketch, "E2.25.18.0", {"center": v(113.38, -29.38) * mm, "radius": 1.88 * mm});
            skCircle(sketch, "E2.25.19.0", {"center": v(113.38, -41.38) * mm, "radius": 1.88 * mm});
            skCircle(sketch, "E2.25.20.0", {"center": v(113.38, -53.38) * mm, "radius": 1.88 * mm});
            skCircle(sketch, "E2.25.21.0", {"center": v(113.38, -65.38) * mm, "radius": 1.88 * mm});
            skCircle(sketch, "E2.25.22.0", {"center": v(113.38, -77.38) * mm, "radius": 1.88 * mm});
            skCircle(sketch, "E2.25.23.0", {"center": v(113.38, -89.38) * mm, "radius": 1.88 * mm});
            skCircle(sketch, "E2.25.24.0", {"center": v(113.38, -101.38) * mm, "radius": 1.88 * mm});
            skCircle(sketch, "E2.25.25.0", {"center": v(113.38, -113.38) * mm, "radius": 1.88 * mm});
            skCircle(sketch, "E2.25.26.0", {"center": v(113.38, -125.38) * mm, "radius": 1.88 * mm});
            skCircle(sketch, "E2.25.27.0", {"center": v(113.38, -137.38) * mm, "radius": 1.88 * mm});
            skCircle(sketch, "E2.25.28.0", {"center": v(113.38, -149.38) * mm, "radius": 1.88 * mm});
            skCircle(sketch, "E2.25.29.0", {"center": v(113.38, -161.38) * mm, "radius": 1.88 * mm});
            skCircle(sketch, "E2.25.30.0", {"center": v(113.38, -173.38) * mm, "radius": 1.88 * mm});
            skCircle(sketch, "E2.25.31.0", {"center": v(113.38, -185.38) * mm, "radius": 1.88 * mm});
            skCircle(sketch, "E2.26.0.0", {"center": v(125.38, 186.62) * mm, "radius": 1.88 * mm});
            skCircle(sketch, "E2.26.1.0", {"center": v(125.38, 174.62) * mm, "radius": 1.88 * mm});
            skCircle(sketch, "E2.26.2.0", {"center": v(125.38, 162.62) * mm, "radius": 1.88 * mm});
            skCircle(sketch, "E2.26.3.0", {"center": v(125.38, 150.62) * mm, "radius": 1.88 * mm});
            skCircle(sketch, "E2.26.4.0", {"center": v(125.38, 138.62) * mm, "radius": 1.88 * mm});
            skCircle(sketch, "E2.26.5.0", {"center": v(125.38, 126.62) * mm, "radius": 1.88 * mm});
            skCircle(sketch, "E2.26.6.0", {"center": v(125.38, 114.62) * mm, "radius": 1.88 * mm});
            skCircle(sketch, "E2.26.7.0", {"center": v(125.38, 102.62) * mm, "radius": 1.88 * mm});
            skCircle(sketch, "E2.26.8.0", {"center": v(125.38, 90.62) * mm, "radius": 1.88 * mm});
            skCircle(sketch, "E2.26.9.0", {"center": v(125.38, 78.62) * mm, "radius": 1.88 * mm});
            skCircle(sketch, "E2.26.10.0", {"center": v(125.38, 66.62) * mm, "radius": 1.88 * mm});
            skCircle(sketch, "E2.26.11.0", {"center": v(125.38, 54.62) * mm, "radius": 1.88 * mm});
            skCircle(sketch, "E2.26.12.0", {"center": v(125.38, 42.62) * mm, "radius": 1.88 * mm});
            skCircle(sketch, "E2.26.13.0", {"center": v(125.38, 30.62) * mm, "radius": 1.88 * mm});
            skCircle(sketch, "E2.26.14.0", {"center": v(125.38, 18.62) * mm, "radius": 1.88 * mm});
            skCircle(sketch, "E2.26.15.0", {"center": v(125.38, 6.62) * mm, "radius": 1.88 * mm});
            skCircle(sketch, "E2.26.16.0", {"center": v(125.38, -5.38) * mm, "radius": 1.88 * mm});
            skCircle(sketch, "E2.26.17.0", {"center": v(125.38, -17.38) * mm, "radius": 1.88 * mm});
            skCircle(sketch, "E2.26.18.0", {"center": v(125.38, -29.38) * mm, "radius": 1.88 * mm});
            skCircle(sketch, "E2.26.19.0", {"center": v(125.38, -41.38) * mm, "radius": 1.88 * mm});
            skCircle(sketch, "E2.26.20.0", {"center": v(125.38, -53.38) * mm, "radius": 1.88 * mm});
            skCircle(sketch, "E2.26.21.0", {"center": v(125.38, -65.38) * mm, "radius": 1.88 * mm});
            skCircle(sketch, "E2.26.22.0", {"center": v(125.38, -77.38) * mm, "radius": 1.88 * mm});
            skCircle(sketch, "E2.26.23.0", {"center": v(125.38, -89.38) * mm, "radius": 1.88 * mm});
            skCircle(sketch, "E2.26.24.0", {"center": v(125.38, -101.38) * mm, "radius": 1.88 * mm});
            skCircle(sketch, "E2.26.25.0", {"center": v(125.38, -113.38) * mm, "radius": 1.88 * mm});
            skCircle(sketch, "E2.26.26.0", {"center": v(125.38, -125.38) * mm, "radius": 1.88 * mm});
            skCircle(sketch, "E2.26.27.0", {"center": v(125.38, -137.38) * mm, "radius": 1.88 * mm});
            skCircle(sketch, "E2.26.28.0", {"center": v(125.38, -149.38) * mm, "radius": 1.88 * mm});
            skCircle(sketch, "E2.26.29.0", {"center": v(125.38, -161.38) * mm, "radius": 1.88 * mm});
            skCircle(sketch, "E2.26.30.0", {"center": v(125.38, -173.38) * mm, "radius": 1.88 * mm});
            skCircle(sketch, "E2.26.31.0", {"center": v(125.38, -185.38) * mm, "radius": 1.88 * mm});
            skCircle(sketch, "E2.27.0.0", {"center": v(137.38, 186.62) * mm, "radius": 1.88 * mm});
            skCircle(sketch, "E2.27.1.0", {"center": v(137.38, 174.62) * mm, "radius": 1.88 * mm});
            skCircle(sketch, "E2.27.2.0", {"center": v(137.38, 162.62) * mm, "radius": 1.88 * mm});
            skCircle(sketch, "E2.27.3.0", {"center": v(137.38, 150.62) * mm, "radius": 1.88 * mm});
            skCircle(sketch, "E2.27.4.0", {"center": v(137.38, 138.62) * mm, "radius": 1.88 * mm});
            skCircle(sketch, "E2.27.5.0", {"center": v(137.38, 126.62) * mm, "radius": 1.88 * mm});
            skCircle(sketch, "E2.27.6.0", {"center": v(137.38, 114.62) * mm, "radius": 1.88 * mm});
            skCircle(sketch, "E2.27.7.0", {"center": v(137.38, 102.62) * mm, "radius": 1.88 * mm});
            skCircle(sketch, "E2.27.8.0", {"center": v(137.38, 90.62) * mm, "radius": 1.88 * mm});
            skCircle(sketch, "E2.27.9.0", {"center": v(137.38, 78.62) * mm, "radius": 1.88 * mm});
            skCircle(sketch, "E2.27.10.0", {"center": v(137.38, 66.62) * mm, "radius": 1.88 * mm});
            skCircle(sketch, "E2.27.11.0", {"center": v(137.38, 54.62) * mm, "radius": 1.88 * mm});
            skCircle(sketch, "E2.27.12.0", {"center": v(137.38, 42.62) * mm, "radius": 1.88 * mm});
            skCircle(sketch, "E2.27.13.0", {"center": v(137.38, 30.62) * mm, "radius": 1.88 * mm});
            skCircle(sketch, "E2.27.14.0", {"center": v(137.38, 18.62) * mm, "radius": 1.88 * mm});
            skCircle(sketch, "E2.27.15.0", {"center": v(137.38, 6.62) * mm, "radius": 1.88 * mm});
            skCircle(sketch, "E2.27.16.0", {"center": v(137.38, -5.38) * mm, "radius": 1.88 * mm});
            skCircle(sketch, "E2.27.17.0", {"center": v(137.38, -17.38) * mm, "radius": 1.88 * mm});
            skCircle(sketch, "E2.27.18.0", {"center": v(137.38, -29.38) * mm, "radius": 1.88 * mm});
            skCircle(sketch, "E2.27.19.0", {"center": v(137.38, -41.38) * mm, "radius": 1.88 * mm});
            skCircle(sketch, "E2.27.20.0", {"center": v(137.38, -53.38) * mm, "radius": 1.88 * mm});
            skCircle(sketch, "E2.27.21.0", {"center": v(137.38, -65.38) * mm, "radius": 1.88 * mm});
            skCircle(sketch, "E2.27.22.0", {"center": v(137.38, -77.38) * mm, "radius": 1.88 * mm});
            skCircle(sketch, "E2.27.23.0", {"center": v(137.38, -89.38) * mm, "radius": 1.88 * mm});
            skCircle(sketch, "E2.27.24.0", {"center": v(137.38, -101.38) * mm, "radius": 1.88 * mm});
            skCircle(sketch, "E2.27.25.0", {"center": v(137.38, -113.38) * mm, "radius": 1.88 * mm});
            skCircle(sketch, "E2.27.26.0", {"center": v(137.38, -125.38) * mm, "radius": 1.88 * mm});
            skCircle(sketch, "E2.27.27.0", {"center": v(137.38, -137.38) * mm, "radius": 1.88 * mm});
            skCircle(sketch, "E2.27.28.0", {"center": v(137.38, -149.38) * mm, "radius": 1.88 * mm});
            skCircle(sketch, "E2.27.29.0", {"center": v(137.38, -161.38) * mm, "radius": 1.88 * mm});
            skCircle(sketch, "E2.27.30.0", {"center": v(137.38, -173.38) * mm, "radius": 1.88 * mm});
            skCircle(sketch, "E2.27.31.0", {"center": v(137.38, -185.38) * mm, "radius": 1.88 * mm});
            skCircle(sketch, "E2.28.0.0", {"center": v(149.38, 186.62) * mm, "radius": 1.88 * mm});
            skCircle(sketch, "E2.28.1.0", {"center": v(149.38, 174.62) * mm, "radius": 1.88 * mm});
            skCircle(sketch, "E2.28.2.0", {"center": v(149.38, 162.62) * mm, "radius": 1.88 * mm});
            skCircle(sketch, "E2.28.3.0", {"center": v(149.38, 150.62) * mm, "radius": 1.88 * mm});
            skCircle(sketch, "E2.28.4.0", {"center": v(149.38, 138.62) * mm, "radius": 1.88 * mm});
            skCircle(sketch, "E2.28.5.0", {"center": v(149.38, 126.62) * mm, "radius": 1.88 * mm});
            skCircle(sketch, "E2.28.6.0", {"center": v(149.38, 114.62) * mm, "radius": 1.88 * mm});
            skCircle(sketch, "E2.28.7.0", {"center": v(149.38, 102.62) * mm, "radius": 1.88 * mm});
            skCircle(sketch, "E2.28.8.0", {"center": v(149.38, 90.62) * mm, "radius": 1.88 * mm});
            skCircle(sketch, "E2.28.9.0", {"center": v(149.38, 78.62) * mm, "radius": 1.88 * mm});
            skCircle(sketch, "E2.28.10.0", {"center": v(149.38, 66.62) * mm, "radius": 1.88 * mm});
            skCircle(sketch, "E2.28.11.0", {"center": v(149.38, 54.62) * mm, "radius": 1.88 * mm});
            skCircle(sketch, "E2.28.12.0", {"center": v(149.38, 42.62) * mm, "radius": 1.88 * mm});
            skCircle(sketch, "E2.28.13.0", {"center": v(149.38, 30.62) * mm, "radius": 1.88 * mm});
            skCircle(sketch, "E2.28.14.0", {"center": v(149.38, 18.62) * mm, "radius": 1.88 * mm});
            skCircle(sketch, "E2.28.15.0", {"center": v(149.38, 6.62) * mm, "radius": 1.88 * mm});
            skCircle(sketch, "E2.28.16.0", {"center": v(149.38, -5.38) * mm, "radius": 1.88 * mm});
            skCircle(sketch, "E2.28.17.0", {"center": v(149.38, -17.38) * mm, "radius": 1.88 * mm});
            skCircle(sketch, "E2.28.18.0", {"center": v(149.38, -29.38) * mm, "radius": 1.88 * mm});
            skCircle(sketch, "E2.28.19.0", {"center": v(149.38, -41.38) * mm, "radius": 1.88 * mm});
            skCircle(sketch, "E2.28.20.0", {"center": v(149.38, -53.38) * mm, "radius": 1.88 * mm});
            skCircle(sketch, "E2.28.21.0", {"center": v(149.38, -65.38) * mm, "radius": 1.88 * mm});
            skCircle(sketch, "E2.28.22.0", {"center": v(149.38, -77.38) * mm, "radius": 1.88 * mm});
            skCircle(sketch, "E2.28.23.0", {"center": v(149.38, -89.38) * mm, "radius": 1.88 * mm});
            skCircle(sketch, "E2.28.24.0", {"center": v(149.38, -101.38) * mm, "radius": 1.88 * mm});
            skCircle(sketch, "E2.28.25.0", {"center": v(149.38, -113.38) * mm, "radius": 1.88 * mm});
            skCircle(sketch, "E2.28.26.0", {"center": v(149.38, -125.38) * mm, "radius": 1.88 * mm});
            skCircle(sketch, "E2.28.27.0", {"center": v(149.38, -137.38) * mm, "radius": 1.88 * mm});
            skCircle(sketch, "E2.28.28.0", {"center": v(149.38, -149.38) * mm, "radius": 1.88 * mm});
            skCircle(sketch, "E2.28.29.0", {"center": v(149.38, -161.38) * mm, "radius": 1.88 * mm});
            skCircle(sketch, "E2.28.30.0", {"center": v(149.38, -173.38) * mm, "radius": 1.88 * mm});
            skCircle(sketch, "E2.28.31.0", {"center": v(149.38, -185.38) * mm, "radius": 1.88 * mm});
            skCircle(sketch, "E2.29.0.0", {"center": v(161.38, 186.62) * mm, "radius": 1.88 * mm});
            skCircle(sketch, "E2.29.1.0", {"center": v(161.38, 174.62) * mm, "radius": 1.88 * mm});
            skCircle(sketch, "E2.29.2.0", {"center": v(161.38, 162.62) * mm, "radius": 1.88 * mm});
            skCircle(sketch, "E2.29.3.0", {"center": v(161.38, 150.62) * mm, "radius": 1.88 * mm});
            skCircle(sketch, "E2.29.4.0", {"center": v(161.38, 138.62) * mm, "radius": 1.88 * mm});
            skCircle(sketch, "E2.29.5.0", {"center": v(161.38, 126.62) * mm, "radius": 1.88 * mm});
            skCircle(sketch, "E2.29.6.0", {"center": v(161.38, 114.62) * mm, "radius": 1.88 * mm});
            skCircle(sketch, "E2.29.7.0", {"center": v(161.38, 102.62) * mm, "radius": 1.88 * mm});
            skCircle(sketch, "E2.29.8.0", {"center": v(161.38, 90.62) * mm, "radius": 1.88 * mm});
            skCircle(sketch, "E2.29.9.0", {"center": v(161.38, 78.62) * mm, "radius": 1.88 * mm});
            skCircle(sketch, "E2.29.10.0", {"center": v(161.38, 66.62) * mm, "radius": 1.88 * mm});
            skCircle(sketch, "E2.29.11.0", {"center": v(161.38, 54.62) * mm, "radius": 1.88 * mm});
            skCircle(sketch, "E2.29.12.0", {"center": v(161.38, 42.62) * mm, "radius": 1.88 * mm});
            skCircle(sketch, "E2.29.13.0", {"center": v(161.38, 30.62) * mm, "radius": 1.88 * mm});
            skCircle(sketch, "E2.29.14.0", {"center": v(161.38, 18.62) * mm, "radius": 1.88 * mm});
            skCircle(sketch, "E2.29.15.0", {"center": v(161.38, 6.62) * mm, "radius": 1.88 * mm});
            skCircle(sketch, "E2.29.16.0", {"center": v(161.38, -5.38) * mm, "radius": 1.88 * mm});
            skCircle(sketch, "E2.29.17.0", {"center": v(161.38, -17.38) * mm, "radius": 1.88 * mm});
            skCircle(sketch, "E2.29.18.0", {"center": v(161.38, -29.38) * mm, "radius": 1.88 * mm});
            skCircle(sketch, "E2.29.19.0", {"center": v(161.38, -41.38) * mm, "radius": 1.88 * mm});
            skCircle(sketch, "E2.29.20.0", {"center": v(161.38, -53.38) * mm, "radius": 1.88 * mm});
            skCircle(sketch, "E2.29.21.0", {"center": v(161.38, -65.38) * mm, "radius": 1.88 * mm});
            skCircle(sketch, "E2.29.22.0", {"center": v(161.38, -77.38) * mm, "radius": 1.88 * mm});
            skCircle(sketch, "E2.29.23.0", {"center": v(161.38, -89.38) * mm, "radius": 1.88 * mm});
            skCircle(sketch, "E2.29.24.0", {"center": v(161.38, -101.38) * mm, "radius": 1.88 * mm});
            skCircle(sketch, "E2.29.25.0", {"center": v(161.38, -113.38) * mm, "radius": 1.88 * mm});
            skCircle(sketch, "E2.29.26.0", {"center": v(161.38, -125.38) * mm, "radius": 1.88 * mm});
            skCircle(sketch, "E2.29.27.0", {"center": v(161.38, -137.38) * mm, "radius": 1.88 * mm});
            skCircle(sketch, "E2.29.28.0", {"center": v(161.38, -149.38) * mm, "radius": 1.88 * mm});
            skCircle(sketch, "E2.29.29.0", {"center": v(161.38, -161.38) * mm, "radius": 1.88 * mm});
            skCircle(sketch, "E2.29.30.0", {"center": v(161.38, -173.38) * mm, "radius": 1.88 * mm});
            skCircle(sketch, "E2.29.31.0", {"center": v(161.38, -185.38) * mm, "radius": 1.88 * mm});
            skCircle(sketch, "E2.30.0.0", {"center": v(173.38, 186.62) * mm, "radius": 1.88 * mm});
            skCircle(sketch, "E2.30.1.0", {"center": v(173.38, 174.62) * mm, "radius": 1.88 * mm});
            skCircle(sketch, "E2.30.2.0", {"center": v(173.38, 162.62) * mm, "radius": 1.88 * mm});
            skCircle(sketch, "E2.30.3.0", {"center": v(173.38, 150.62) * mm, "radius": 1.88 * mm});
            skCircle(sketch, "E2.30.4.0", {"center": v(173.38, 138.62) * mm, "radius": 1.88 * mm});
            skCircle(sketch, "E2.30.5.0", {"center": v(173.38, 126.62) * mm, "radius": 1.88 * mm});
            skCircle(sketch, "E2.30.6.0", {"center": v(173.38, 114.62) * mm, "radius": 1.88 * mm});
            skCircle(sketch, "E2.30.7.0", {"center": v(173.38, 102.62) * mm, "radius": 1.88 * mm});
            skCircle(sketch, "E2.30.8.0", {"center": v(173.38, 90.62) * mm, "radius": 1.88 * mm});
            skCircle(sketch, "E2.30.9.0", {"center": v(173.38, 78.62) * mm, "radius": 1.88 * mm});
            skCircle(sketch, "E2.30.10.0", {"center": v(173.38, 66.62) * mm, "radius": 1.88 * mm});
            skCircle(sketch, "E2.30.11.0", {"center": v(173.38, 54.62) * mm, "radius": 1.88 * mm});
            skCircle(sketch, "E2.30.12.0", {"center": v(173.38, 42.62) * mm, "radius": 1.88 * mm});
            skCircle(sketch, "E2.30.13.0", {"center": v(173.38, 30.62) * mm, "radius": 1.88 * mm});
            skCircle(sketch, "E2.30.14.0", {"center": v(173.38, 18.62) * mm, "radius": 1.88 * mm});
            skCircle(sketch, "E2.30.15.0", {"center": v(173.38, 6.62) * mm, "radius": 1.88 * mm});
            skCircle(sketch, "E2.30.16.0", {"center": v(173.38, -5.38) * mm, "radius": 1.88 * mm});
            skCircle(sketch, "E2.30.17.0", {"center": v(173.38, -17.38) * mm, "radius": 1.88 * mm});
            skCircle(sketch, "E2.30.18.0", {"center": v(173.38, -29.38) * mm, "radius": 1.88 * mm});
            skCircle(sketch, "E2.30.19.0", {"center": v(173.38, -41.38) * mm, "radius": 1.88 * mm});
            skCircle(sketch, "E2.30.20.0", {"center": v(173.38, -53.38) * mm, "radius": 1.88 * mm});
            skCircle(sketch, "E2.30.21.0", {"center": v(173.38, -65.38) * mm, "radius": 1.88 * mm});
            skCircle(sketch, "E2.30.22.0", {"center": v(173.38, -77.38) * mm, "radius": 1.88 * mm});
            skCircle(sketch, "E2.30.23.0", {"center": v(173.38, -89.38) * mm, "radius": 1.88 * mm});
            skCircle(sketch, "E2.30.24.0", {"center": v(173.38, -101.38) * mm, "radius": 1.88 * mm});
            skCircle(sketch, "E2.30.25.0", {"center": v(173.38, -113.38) * mm, "radius": 1.88 * mm});
            skCircle(sketch, "E2.30.26.0", {"center": v(173.38, -125.38) * mm, "radius": 1.88 * mm});
            skCircle(sketch, "E2.30.27.0", {"center": v(173.38, -137.38) * mm, "radius": 1.88 * mm});
            skCircle(sketch, "E2.30.28.0", {"center": v(173.38, -149.38) * mm, "radius": 1.88 * mm});
            skCircle(sketch, "E2.30.29.0", {"center": v(173.38, -161.38) * mm, "radius": 1.88 * mm});
            skCircle(sketch, "E2.30.30.0", {"center": v(173.38, -173.38) * mm, "radius": 1.88 * mm});
            skCircle(sketch, "E2.30.31.0", {"center": v(173.38, -185.38) * mm, "radius": 1.88 * mm});
            skCircle(sketch, "E2.31.0.0", {"center": v(185.38, 186.62) * mm, "radius": 1.88 * mm});
            skCircle(sketch, "E2.31.1.0", {"center": v(185.38, 174.62) * mm, "radius": 1.88 * mm});
            skCircle(sketch, "E2.31.2.0", {"center": v(185.38, 162.62) * mm, "radius": 1.88 * mm});
            skCircle(sketch, "E2.31.3.0", {"center": v(185.38, 150.62) * mm, "radius": 1.88 * mm});
            skCircle(sketch, "E2.31.4.0", {"center": v(185.38, 138.62) * mm, "radius": 1.88 * mm});
            skCircle(sketch, "E2.31.5.0", {"center": v(185.38, 126.62) * mm, "radius": 1.88 * mm});
            skCircle(sketch, "E2.31.6.0", {"center": v(185.38, 114.62) * mm, "radius": 1.88 * mm});
            skCircle(sketch, "E2.31.7.0", {"center": v(185.38, 102.62) * mm, "radius": 1.88 * mm});
            skCircle(sketch, "E2.31.8.0", {"center": v(185.38, 90.62) * mm, "radius": 1.88 * mm});
            skCircle(sketch, "E2.31.9.0", {"center": v(185.38, 78.62) * mm, "radius": 1.88 * mm});
            skCircle(sketch, "E2.31.10.0", {"center": v(185.38, 66.62) * mm, "radius": 1.88 * mm});
            skCircle(sketch, "E2.31.11.0", {"center": v(185.38, 54.62) * mm, "radius": 1.88 * mm});
            skCircle(sketch, "E2.31.12.0", {"center": v(185.38, 42.62) * mm, "radius": 1.88 * mm});
            skCircle(sketch, "E2.31.13.0", {"center": v(185.38, 30.62) * mm, "radius": 1.88 * mm});
            skCircle(sketch, "E2.31.14.0", {"center": v(185.38, 18.62) * mm, "radius": 1.88 * mm});
            skCircle(sketch, "E2.31.15.0", {"center": v(185.38, 6.62) * mm, "radius": 1.88 * mm});
            skCircle(sketch, "E2.31.16.0", {"center": v(185.38, -5.38) * mm, "radius": 1.88 * mm});
            skCircle(sketch, "E2.31.17.0", {"center": v(185.38, -17.38) * mm, "radius": 1.88 * mm});
            skCircle(sketch, "E2.31.18.0", {"center": v(185.38, -29.38) * mm, "radius": 1.88 * mm});
            skCircle(sketch, "E2.31.19.0", {"center": v(185.38, -41.38) * mm, "radius": 1.88 * mm});
            skCircle(sketch, "E2.31.20.0", {"center": v(185.38, -53.38) * mm, "radius": 1.88 * mm});
            skCircle(sketch, "E2.31.21.0", {"center": v(185.38, -65.38) * mm, "radius": 1.88 * mm});
            skCircle(sketch, "E2.31.22.0", {"center": v(185.38, -77.38) * mm, "radius": 1.88 * mm});
            skCircle(sketch, "E2.31.23.0", {"center": v(185.38, -89.38) * mm, "radius": 1.88 * mm});
            skCircle(sketch, "E2.31.24.0", {"center": v(185.38, -101.38) * mm, "radius": 1.88 * mm});
            skCircle(sketch, "E2.31.25.0", {"center": v(185.38, -113.38) * mm, "radius": 1.88 * mm});
            skCircle(sketch, "E2.31.26.0", {"center": v(185.38, -125.38) * mm, "radius": 1.88 * mm});
            skCircle(sketch, "E2.31.27.0", {"center": v(185.38, -137.38) * mm, "radius": 1.88 * mm});
            skCircle(sketch, "E2.31.28.0", {"center": v(185.38, -149.38) * mm, "radius": 1.88 * mm});
            skCircle(sketch, "E2.31.29.0", {"center": v(185.38, -161.38) * mm, "radius": 1.88 * mm});
            skCircle(sketch, "E2.31.30.0", {"center": v(185.38, -173.38) * mm, "radius": 1.88 * mm});
            skCircle(sketch, "E2.31.31.0", {"center": v(185.38, -185.38) * mm, "radius": 1.88 * mm});
            skLineSegment(sketch, "E2.direction1", {"start": v(-186.63, 186.62) * mm, "end": v(-174.63, 186.62) * mm, "construction": true});
            skLineSegment(sketch, "E2.direction2", {"start": v(-186.63, 186.62) * mm, "end": v(-186.63, 174.62) * mm, "construction": true});
            skSolve(sketch);
        }
        {
            var Q0;
            Q0=makeQuery(id+"F1.opExtrude","CAP_FACE",FACE,{"disambiguationData":[OSD([sQuery(id+"F0.wireOp",EDGE,"E0.bottom"),sQuery(id+"F0.wireOp",EDGE,"E0.top"),sQuery(id+"F0.wireOp",EDGE,"E0.left"),sQuery(id+"F0.wireOp",EDGE,"E0.right")])],"isStart":true});
            var sketch = newSketch(context, id + "F3", { "sketchPlane" : qUnion([Q0])});
            skLineSegment(sketch, "E3.0", {"start": v(198.5, 198.5) * mm, "end": v(-198.5, 198.5) * mm});
            skLineSegment(sketch, "E3.1", {"start": v(198.5, -198.5) * mm, "end": v(198.5, 198.5) * mm});
            skLineSegment(sketch, "E3.2", {"start": v(-198.5, -198.5) * mm, "end": v(198.5, -198.5) * mm});
            skLineSegment(sketch, "E3.3", {"start": v(-198.5, 198.5) * mm, "end": v(-198.5, -198.5) * mm});
            skSolve(sketch);
        }
        {
            var Q0;
            Q0=makeQuery(id+"F3.imprint","IMPRINT",FACE,{"disambiguationData":[TD([[makeQuery(id+"F3.imprint","IMPRINT",EDGE,{"derivedFrom":sQuery(id+"F3.wireOp",EDGE,"E3.0")}),-1.0]])]});
            extrude(context, id + "F4", {"entities" : qUnion([Q0]), "operationType" : NewBodyOperationType.ADD, "depth" : 15.5 * mm, "offsetDistance" : 25 * mm});
        }
        {
            var Q0;
            Q0=makeQuery(id+"F4.opExtrude","SWEPT_FACE",FACE,{"disambiguationData":[OSD([sQuery(id+"F3.wireOp",EDGE,"E3.0")])]});
            extrude(context, id + "F5", {"entities" : qUnion([Q0]), "operationType" : NewBodyOperationType.ADD, "depth" : (12 - 1.5) * mm, "offsetDistance" : 25 * mm});
        }
        {
            var Q0;
            Q0=makeQuery(id+"F4.opExtrude","SWEPT_FACE",FACE,{"disambiguationData":[OSD([sQuery(id+"F3.wireOp",EDGE,"E3.2")])]});
            extrude(context, id + "F6", {"entities" : qUnion([Q0]), "operationType" : NewBodyOperationType.ADD, "depth" : (12 - 1.5) * mm, "offsetDistance" : 25 * mm});
        }
        {
            var Q0;
            Q0 = qSketchRegion(id + "F2", true);
            extrude(context, id + "F7", {"entities" : qUnion([Q0]), "operationType" : NewBodyOperationType.REMOVE, "endBound" : BoundingType.UP_TO_NEXT, "oppositeDirection" : true, "depth" : 25 * mm, "offsetDistance" : 25 * mm});
        }
    });
